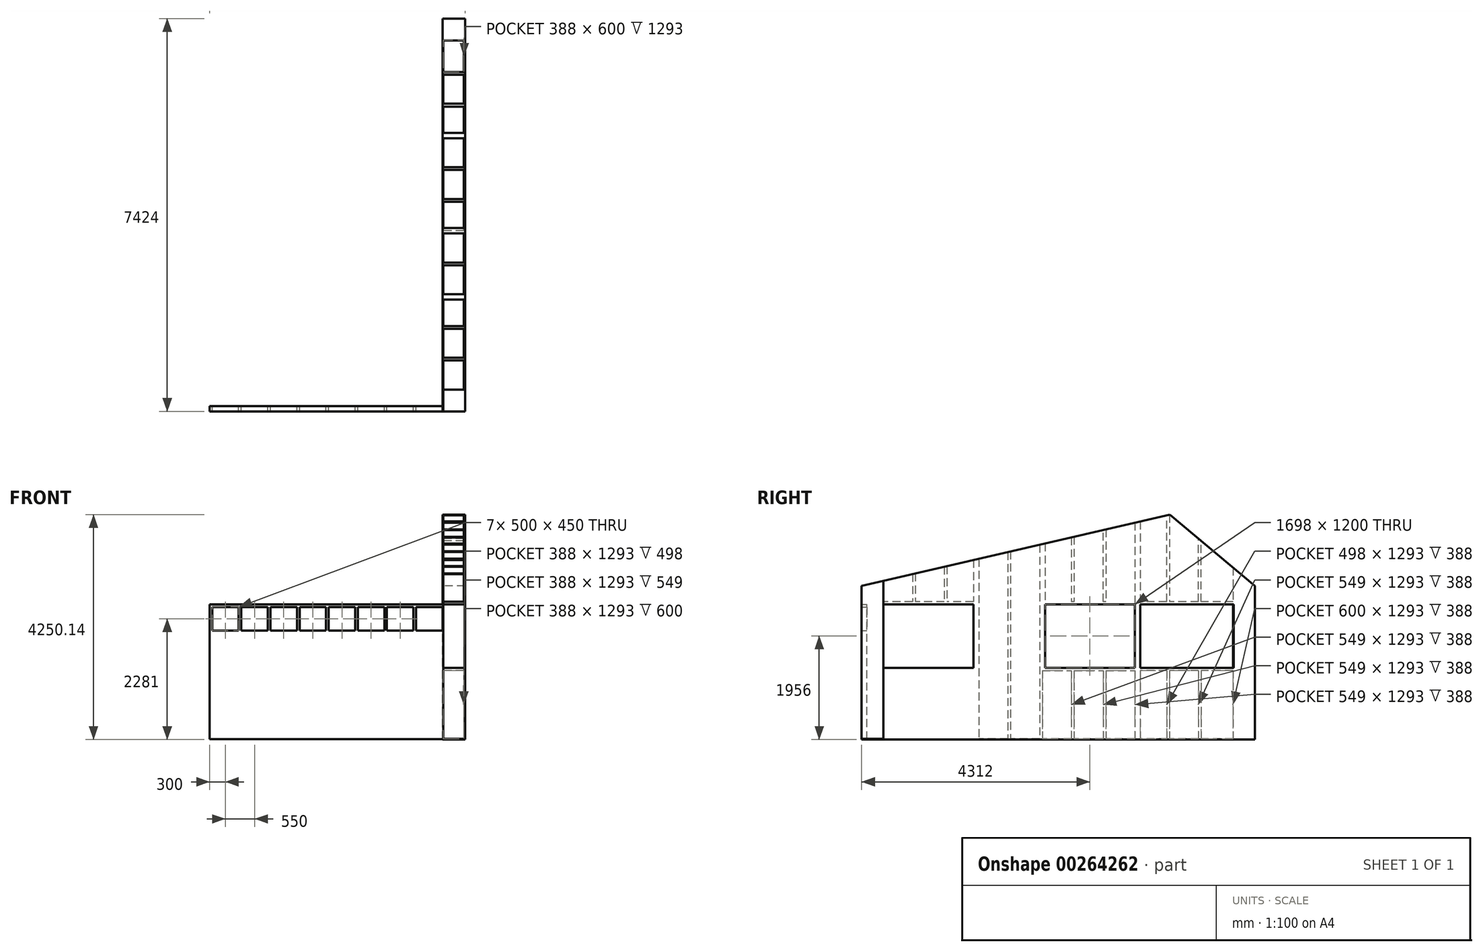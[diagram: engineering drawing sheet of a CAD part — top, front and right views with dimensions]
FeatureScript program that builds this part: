
annotation { "Feature Type Name" : "Feature", "Feature Type Description" : "" }
export const myFeature = defineFeature(function(context is Context, id is Id, definition is map)
    precondition{}
    {
        {
            var Q0;
            Q0=qCreatedBy(makeId("Right.planeOp"),FACE);
            var sketch = newSketch(context, id + "F0", { "sketchPlane" : qUnion([Q0])});
            skLineSegment(sketch, "E0.bottom", {"start": v(0, 0) * mm, "end": v(2161, 0) * mm});
            skLineSegment(sketch, "E0.top", {"start": v(412, 2900) * mm, "end": v(961, 2900) * mm});
            skLineSegment(sketch, "E0.left", {"start": v(0, 0) * mm, "end": v(0, 2900) * mm});
            skLineSegment(sketch, "E0.right", {"start": v(7424, 0) * mm, "end": v(7424, 2900) * mm});
            skLineSegment(sketch, "E1", {"start": v(7424, 2900) * mm, "end": v(5822.11, 4244.14) * mm});
            skLineSegment(sketch, "E2", {"start": v(5822.11, 4244.14) * mm, "end": v(0, 2900) * mm});
            skLineSegment(sketch, "E3", {"start": v(412, 2995.12) * mm, "end": v(412, 0) * mm});
            skLineSegment(sketch, "E4", {"start": v(7012, 3245.7) * mm, "end": v(7012, 0) * mm});
            skLineSegment(sketch, "E5.bottom", {"start": v(961, 2900) * mm, "end": v(1012, 2900) * mm});
            skLineSegment(sketch, "E5.top", {"start": v(961, 0) * mm, "end": v(1012, 0) * mm});
            skLineSegment(sketch, "E5.left", {"start": v(961, 2900) * mm, "end": v(961, 2601) * mm});
            skLineSegment(sketch, "E5.right", {"start": v(1012, 2900) * mm, "end": v(1012, 2601) * mm});
            skLineSegment(sketch, "E6.1.0.0", {"start": v(1561, 2900) * mm, "end": v(1561, 2601) * mm});
            skLineSegment(sketch, "E6.1.0.1", {"start": v(1612, 2900) * mm, "end": v(1612, 2601) * mm});
            skLineSegment(sketch, "E6.1.0.2", {"start": v(1561, 2900) * mm, "end": v(1612, 2900) * mm});
            skLineSegment(sketch, "E6.1.0.3", {"start": v(1561, 0) * mm, "end": v(1612, 0) * mm});
            skLineSegment(sketch, "E6.2.0.0", {"start": v(2161, 2900) * mm, "end": v(2161, 0) * mm});
            skLineSegment(sketch, "E6.2.0.1", {"start": v(2212, 2900) * mm, "end": v(2212, 0) * mm});
            skLineSegment(sketch, "E6.2.0.2", {"start": v(2161, 2900) * mm, "end": v(2212, 2900) * mm});
            skLineSegment(sketch, "E6.2.0.3", {"start": v(2161, 0) * mm, "end": v(2212, 0) * mm});
            skLineSegment(sketch, "E6.3.0.0", {"start": v(2761, 2900) * mm, "end": v(2761, 0) * mm});
            skLineSegment(sketch, "E6.3.0.1", {"start": v(2812, 2900) * mm, "end": v(2812, 0) * mm});
            skLineSegment(sketch, "E6.3.0.2", {"start": v(2761, 2900) * mm, "end": v(2812, 2900) * mm});
            skLineSegment(sketch, "E6.3.0.3", {"start": v(2761, 0) * mm, "end": v(2812, 0) * mm});
            skLineSegment(sketch, "E6.4.0.0", {"start": v(3361, 2900) * mm, "end": v(3361, 0) * mm});
            skLineSegment(sketch, "E6.4.0.1", {"start": v(3412, 3687.72) * mm, "end": v(3412, 0) * mm});
            skLineSegment(sketch, "E6.4.0.2", {"start": v(3361, 2900) * mm, "end": v(3412, 2900) * mm});
            skLineSegment(sketch, "E6.direction1", {"start": v(961, 0) * mm, "end": v(1561, 0) * mm, "construction": true});
            skLineSegment(sketch, "E7", {"start": v(961, 2900) * mm, "end": v(961, 3121.86) * mm});
            skLineSegment(sketch, "E8", {"start": v(961, 3121.86) * mm, "end": v(1012, 3133.64) * mm});
            skLineSegment(sketch, "E9", {"start": v(1012, 3133.64) * mm, "end": v(1012, 2900) * mm});
            skLineSegment(sketch, "E10", {"start": v(1561, 2900) * mm, "end": v(1561, 3260.39) * mm});
            skLineSegment(sketch, "E11", {"start": v(1561, 3260.39) * mm, "end": v(1612, 3272.16) * mm});
            skLineSegment(sketch, "E12", {"start": v(1612, 3272.16) * mm, "end": v(1612, 2900) * mm});
            skLineSegment(sketch, "E13", {"start": v(2161, 2900) * mm, "end": v(2161, 3398.9) * mm});
            skLineSegment(sketch, "E14", {"start": v(2161, 3398.9) * mm, "end": v(2212, 3410.68) * mm});
            skLineSegment(sketch, "E15", {"start": v(2212, 3410.68) * mm, "end": v(2212, 2900) * mm});
            skLineSegment(sketch, "E16", {"start": v(2761, 2900) * mm, "end": v(2761, 3537.43) * mm});
            skLineSegment(sketch, "E17", {"start": v(2761, 3537.43) * mm, "end": v(2812, 3549.2) * mm});
            skLineSegment(sketch, "E18", {"start": v(2812, 3549.2) * mm, "end": v(2812, 2900) * mm});
            skLineSegment(sketch, "E19", {"start": v(3361, 2900) * mm, "end": v(3361, 3675.95) * mm});
            skLineSegment(sketch, "E20", {"start": v(3361, 3675.95) * mm, "end": v(3412, 3687.72) * mm});
            skLineSegment(sketch, "E21", {"start": v(3961, 3814.47) * mm, "end": v(3961, 3814.47) * mm});
            skLineSegment(sketch, "E22", {"start": v(3961, 3814.47) * mm, "end": v(4012, 3826.24) * mm});
            skLineSegment(sketch, "E23", {"start": v(4012, 3826.24) * mm, "end": v(4012, 3826.24) * mm});
            skLineSegment(sketch, "E24.bottom", {"start": v(7012, 0) * mm, "end": v(6412, 0) * mm});
            skLineSegment(sketch, "E25.bottom", {"start": v(2110, 2550) * mm, "end": v(412, 2550) * mm});
            skLineSegment(sketch, "E25.top", {"start": v(2110, 1350) * mm, "end": v(412, 1350) * mm});
            skLineSegment(sketch, "E26.bottom", {"start": v(2110, 2601) * mm, "end": v(412, 2601) * mm});
            skLineSegment(sketch, "E26.top", {"start": v(2110, 1299) * mm, "end": v(412, 1299) * mm});
            skLineSegment(sketch, "E27", {"start": v(2110, 3387.13) * mm, "end": v(2110, 0) * mm});
            skLineSegment(sketch, "E28", {"start": v(4561, 2601) * mm, "end": v(4561, 3952.99) * mm});
            skLineSegment(sketch, "E29", {"start": v(4561, 3952.99) * mm, "end": v(4612, 3964.76) * mm});
            skLineSegment(sketch, "E30", {"start": v(4612, 3964.76) * mm, "end": v(4612, 2601) * mm});
            skLineSegment(sketch, "E31.9.9.0", {"start": v(6361, 0) * mm, "end": v(6412, 0) * mm});
            skLineSegment(sketch, "E32", {"start": v(5761, 2601) * mm, "end": v(5761, 4295.42) * mm});
            skLineSegment(sketch, "E33", {"start": v(6361, 2601) * mm, "end": v(6361, 3791.96) * mm});
            skLineSegment(sketch, "E34", {"start": v(6412, 2601) * mm, "end": v(6412, 3749.17) * mm});
            skLineSegment(sketch, "E35.top", {"start": v(4012, 0) * mm, "end": v(4012, 0) * mm});
            skLineSegment(sketch, "E36.top", {"start": v(7012, 1350) * mm, "end": v(5263, 1350) * mm});
            skLineSegment(sketch, "E37.top", {"start": v(7012, 1299) * mm, "end": v(5263, 1299) * mm});
            skLineSegment(sketch, "E37.left", {"start": v(7012, 2601) * mm, "end": v(7012, 1299) * mm});
            skLineSegment(sketch, "E38.right", {"start": v(4012, 3826.24) * mm, "end": v(4012, 2601) * mm});
            skLineSegment(sketch, "E39.right", {"start": v(5161, 4091.51) * mm, "end": v(5161, 1350) * mm});
            skLineSegment(sketch, "E40", {"start": v(3961, 3814.47) * mm, "end": v(3961, 2601) * mm});
            skLineSegment(sketch, "E41.trimOffspring", {"start": v(4012, 0) * mm, "end": v(7424, 0) * mm});
            skLineSegment(sketch, "E42.trimOffspring", {"start": v(3961, 0) * mm, "end": v(3412, 0) * mm});
            skLineSegment(sketch, "E43.trimOffspring", {"start": v(6361, 0) * mm, "end": v(4012, 0) * mm});
            skLineSegment(sketch, "E44.trimOffspring", {"start": v(3412, 0) * mm, "end": v(3961, 0) * mm});
            skLineSegment(sketch, "E45.trimOffspring", {"start": v(3361, 0) * mm, "end": v(412, 0) * mm});
            skLineSegment(sketch, "E46", {"start": v(3412, 0) * mm, "end": v(3361, 0) * mm});
            skLineSegment(sketch, "E47", {"start": v(4012, 0) * mm, "end": v(3961, 0) * mm});
            skLineSegment(sketch, "E48.trimOffspring", {"start": v(2812, 0) * mm, "end": v(3361, 0) * mm});
            skLineSegment(sketch, "E49.trimOffspring", {"start": v(2212, 0) * mm, "end": v(2761, 0) * mm});
            skLineSegment(sketch, "E50.trimOffspring", {"start": v(6412, 1299) * mm, "end": v(6412, 0) * mm});
            skLineSegment(sketch, "E51.trimOffspring", {"start": v(6361, 1299) * mm, "end": v(6361, 0) * mm});
            skLineSegment(sketch, "E52", {"start": v(5212, 4103.29) * mm, "end": v(5212, 0) * mm});
            skLineSegment(sketch, "E53", {"start": v(5812, 4252.63) * mm, "end": v(5812, 2601) * mm});
            skLineSegment(sketch, "E54.trimOffspring", {"start": v(961, 1299) * mm, "end": v(961, 0) * mm});
            skLineSegment(sketch, "E55.trimOffspring", {"start": v(1012, 1299) * mm, "end": v(1012, 0) * mm});
            skLineSegment(sketch, "E56.trimOffspring", {"start": v(1561, 2900) * mm, "end": v(2110, 2900) * mm});
            skLineSegment(sketch, "E57", {"start": v(5812, 1299) * mm, "end": v(5812, 0) * mm});
            skLineSegment(sketch, "E58", {"start": v(5761, 1299) * mm, "end": v(5761, 0) * mm});
            skLineSegment(sketch, "E59", {"start": v(4612, 2550) * mm, "end": v(4561, 2550) * mm});
            skLineSegment(sketch, "E60", {"start": v(7012, 2601) * mm, "end": v(5263, 2601) * mm});
            skLineSegment(sketch, "E61", {"start": v(7012, 2550) * mm, "end": v(5263, 2550) * mm});
            skLineSegment(sketch, "E62", {"start": v(5212, 2550) * mm, "end": v(3463, 2550) * mm});
            skLineSegment(sketch, "E63", {"start": v(3463, 1350) * mm, "end": v(5161, 1350) * mm});
            skLineSegment(sketch, "E64", {"start": v(5161, 2601) * mm, "end": v(3463, 2601) * mm});
            skLineSegment(sketch, "E65", {"start": v(3412, 1299) * mm, "end": v(5161, 1299) * mm});
            skLineSegment(sketch, "E66", {"start": v(4561, 1299) * mm, "end": v(4561, 0) * mm});
            skLineSegment(sketch, "E67", {"start": v(4612, 1299) * mm, "end": v(4612, 0) * mm});
            skLineSegment(sketch, "E68.trimOffspring", {"start": v(5161, 1299) * mm, "end": v(5161, 0) * mm});
            skLineSegment(sketch, "E69", {"start": v(3412, 1299) * mm, "end": v(3412, 0) * mm});
            skLineSegment(sketch, "E70", {"start": v(3463, 3699.5) * mm, "end": v(3463, 0) * mm});
            skLineSegment(sketch, "E71", {"start": v(5263, 4115.06) * mm, "end": v(5263, 0) * mm});
            skLineSegment(sketch, "E72.trimOffspring", {"start": v(4012, 1299) * mm, "end": v(4012, 0) * mm});
            skLineSegment(sketch, "E73.trimOffspring", {"start": v(3961, 1299) * mm, "end": v(3961, 0) * mm});
            skLineSegment(sketch, "E74.trimOffspring", {"start": v(1612, 1299) * mm, "end": v(1612, 0) * mm});
            skLineSegment(sketch, "E75.trimOffspring", {"start": v(1561, 1299) * mm, "end": v(1561, 0) * mm});
            skSolve(sketch);
        }
        {
            var Q0;
            {var subQ0=sQuery(id+"F0.wireOp",EDGE,"E33");Q0=makeQuery(id+"F0.imprint","IMPRINT",FACE,{"disambiguationData":[TD([[makeQuery(id+"F0.imprint","IMPRINT",EDGE,{"derivedFrom":subQ0}),-1.0]])]});}
            var Q1;
            {var subQ0=sQuery(id+"F0.wireOp",EDGE,"E53");var subQ1=sQuery(id+"F0.wireOp",EDGE,"E2");var subQ2=makeQuery(id+"F0.imprint","INTERSECT",VERTEX,{"derivedFrom":[subQ1,subQ0]});Q1=makeQuery(id+"F0.imprint","IMPRINT",FACE,{"disambiguationData":[TD([[makeQuery(id+"F0.imprint","IMPRINT",EDGE,{"disambiguationData":[TD([[subQ2,-1.0]])],"derivedFrom":subQ1}),1.0]])]});}
            var Q2;
            {var subQ0=sQuery(id+"F0.wireOp",EDGE,"E33");Q2=makeQuery(id+"F0.imprint","IMPRINT",FACE,{"disambiguationData":[TD([[makeQuery(id+"F0.imprint","IMPRINT",EDGE,{"derivedFrom":subQ0}),-1.0]])]});}
            var Q3;
            {var subQ0=sQuery(id+"F0.wireOp",EDGE,"E53");var subQ1=sQuery(id+"F0.wireOp",EDGE,"E2");var subQ2=makeQuery(id+"F0.imprint","INTERSECT",VERTEX,{"derivedFrom":[subQ1,subQ0]});Q3=makeQuery(id+"F0.imprint","IMPRINT",FACE,{"disambiguationData":[TD([[makeQuery(id+"F0.imprint","IMPRINT",EDGE,{"disambiguationData":[TD([[subQ2,-1.0]])],"derivedFrom":subQ1}),1.0]])]});}
            var Q4;
            {var subQ0=sQuery(id+"F0.wireOp",EDGE,"E38.top");Q4=makeQuery(id+"F0.imprint","IMPRINT",FACE,{"disambiguationData":[TD([[makeQuery(id+"F0.imprint","IMPRINT",EDGE,{"derivedFrom":subQ0}),1.0]])]});}
            var Q5;
            {var subQ0=sQuery(id+"F0.wireOp",EDGE,"E38.top");Q5=makeQuery(id+"F0.imprint","IMPRINT",FACE,{"disambiguationData":[TD([[makeQuery(id+"F0.imprint","IMPRINT",EDGE,{"derivedFrom":subQ0}),1.0]])]});}
            var Q6;
            {var subQ0=sQuery(id+"F0.wireOp",EDGE,"E6.2.0.0");Q6=makeQuery(id+"F0.imprint","IMPRINT",FACE,{"disambiguationData":[TD([[makeQuery(id+"F0.imprint","IMPRINT",EDGE,{"derivedFrom":subQ0}),1.0]])]});}
            var Q7;
            {var subQ0=sQuery(id+"F0.wireOp",EDGE,"E6.3.0.0");Q7=makeQuery(id+"F0.imprint","IMPRINT",FACE,{"disambiguationData":[TD([[makeQuery(id+"F0.imprint","IMPRINT",EDGE,{"derivedFrom":subQ0}),1.0]])]});}
            var Q8;
            Q8=makeQuery(id+"F0.imprint","IMPRINT",FACE,{"disambiguationData":[TD([[makeQuery(id+"F0.imprint","IMPRINT",EDGE,{"derivedFrom":sQuery(id+"F0.wireOp",EDGE,"E6.4.0.0")}),1.0]])]});
            var Q9;
            {var subQ0=sQuery(id+"F0.wireOp",EDGE,"E50.trimOffspring");Q9=makeQuery(id+"F0.imprint","IMPRINT",FACE,{"disambiguationData":[TD([[makeQuery(id+"F0.imprint","IMPRINT",EDGE,{"derivedFrom":subQ0}),-1.0]])]});}
            var Q10;
            {var subQ0=sQuery(id+"F0.wireOp",EDGE,"E57");Q10=makeQuery(id+"F0.imprint","IMPRINT",FACE,{"disambiguationData":[TD([[makeQuery(id+"F0.imprint","IMPRINT",EDGE,{"derivedFrom":subQ0}),-1.0]])]});}
            var Q11;
            {var subQ4=sQuery(id+"F0.wireOp",EDGE,"E25.bottom");Q11=makeQuery(id+"F0.imprint","IMPRINT",FACE,{"disambiguationData":[TD([[makeQuery(id+"F0.imprint","IMPRINT",EDGE,{"derivedFrom":subQ4}),-1.0]])]});}
            var Q12;
            {var subQ0=sQuery(id+"F0.wireOp",EDGE,"E5.left");Q12=makeQuery(id+"F0.imprint","IMPRINT",FACE,{"disambiguationData":[TD([[makeQuery(id+"F0.imprint","IMPRINT",EDGE,{"derivedFrom":subQ0}),1.0]])]});}
            var Q13;
            {var subQ0=sQuery(id+"F0.wireOp",EDGE,"E33");Q13=makeQuery(id+"F0.imprint","IMPRINT",FACE,{"disambiguationData":[TD([[makeQuery(id+"F0.imprint","IMPRINT",EDGE,{"derivedFrom":subQ0}),-1.0]])]});}
            var Q14;
            {var subQ0=sQuery(id+"F0.wireOp",EDGE,"E53");var subQ1=sQuery(id+"F0.wireOp",EDGE,"E2");var subQ2=makeQuery(id+"F0.imprint","INTERSECT",VERTEX,{"derivedFrom":[subQ1,subQ0]});Q14=makeQuery(id+"F0.imprint","IMPRINT",FACE,{"disambiguationData":[TD([[makeQuery(id+"F0.imprint","IMPRINT",EDGE,{"disambiguationData":[TD([[subQ2,-1.0]])],"derivedFrom":subQ1}),1.0]])]});}
            var Q15;
            {var subQ0=sQuery(id+"F0.wireOp",EDGE,"E53");var subQ1=sQuery(id+"F0.wireOp",EDGE,"E2");var subQ2=makeQuery(id+"F0.imprint","INTERSECT",VERTEX,{"derivedFrom":[subQ1,subQ0]});Q15=makeQuery(id+"F0.imprint","IMPRINT",FACE,{"disambiguationData":[TD([[makeQuery(id+"F0.imprint","IMPRINT",EDGE,{"disambiguationData":[TD([[subQ2,-1.0]])],"derivedFrom":subQ1}),1.0]])]});}
            var Q16;
            {var subQ0=sQuery(id+"F0.wireOp",EDGE,"E5.left");Q16=makeQuery(id+"F0.imprint","IMPRINT",FACE,{"disambiguationData":[TD([[makeQuery(id+"F0.imprint","IMPRINT",EDGE,{"derivedFrom":subQ0}),1.0]])]});}
            var Q17;
            {var subQ0=sQuery(id+"F0.wireOp",EDGE,"E6.3.0.0");Q17=makeQuery(id+"F0.imprint","IMPRINT",FACE,{"disambiguationData":[TD([[makeQuery(id+"F0.imprint","IMPRINT",EDGE,{"derivedFrom":subQ0}),1.0]])]});}
            var Q18;
            {var subQ0=sQuery(id+"F0.wireOp",EDGE,"E38.top");Q18=makeQuery(id+"F0.imprint","IMPRINT",FACE,{"disambiguationData":[TD([[makeQuery(id+"F0.imprint","IMPRINT",EDGE,{"derivedFrom":subQ0}),1.0]])]});}
            var Q19;
            {var subQ0=sQuery(id+"F0.wireOp",EDGE,"E6.2.0.0");Q19=makeQuery(id+"F0.imprint","IMPRINT",FACE,{"disambiguationData":[TD([[makeQuery(id+"F0.imprint","IMPRINT",EDGE,{"derivedFrom":subQ0}),1.0]])]});}
            var Q20;
            Q20=makeQuery(id+"F0.imprint","IMPRINT",FACE,{"disambiguationData":[TD([[makeQuery(id+"F0.imprint","IMPRINT",EDGE,{"derivedFrom":sQuery(id+"F0.wireOp",EDGE,"E6.4.0.0")}),1.0]])]});
            var Q21;
            {var subQ9=sQuery(id+"F0.wireOp",EDGE,"E6.1.0.1");Q21=makeQuery(id+"F0.imprint","IMPRINT",FACE,{"disambiguationData":[TD([[makeQuery(id+"F0.imprint","IMPRINT",EDGE,{"derivedFrom":subQ9}),-1.0]])]});}
            var Q22;
            {var subQ0=sQuery(id+"F0.wireOp",EDGE,"E5.left");Q22=makeQuery(id+"F0.imprint","IMPRINT",FACE,{"disambiguationData":[TD([[makeQuery(id+"F0.imprint","IMPRINT",EDGE,{"derivedFrom":subQ0}),1.0]])]});}
            var Q23;
            {var subQ0=sQuery(id+"F0.wireOp",EDGE,"E5.left");Q23=makeQuery(id+"F0.imprint","IMPRINT",FACE,{"disambiguationData":[TD([[makeQuery(id+"F0.imprint","IMPRINT",EDGE,{"derivedFrom":subQ0}),1.0]])]});}
            var Q24;
            {var subQ6=sQuery(id+"F0.wireOp",EDGE,"E36.bottom");Q24=makeQuery(id+"F0.imprint","IMPRINT",FACE,{"disambiguationData":[TD([[makeQuery(id+"F0.imprint","IMPRINT",EDGE,{"derivedFrom":subQ6}),-1.0]])]});}
            var Q25;
            {var subQ5=sQuery(id+"F0.wireOp",EDGE,"E39.right");Q25=makeQuery(id+"F0.imprint","IMPRINT",FACE,{"disambiguationData":[TD([[makeQuery(id+"F0.imprint","IMPRINT",EDGE,{"derivedFrom":subQ5}),1.0]])]});}
            var Q26;
            {var subQ0=sQuery(id+"F0.wireOp",EDGE,"E28");Q26=makeQuery(id+"F0.imprint","IMPRINT",FACE,{"disambiguationData":[TD([[makeQuery(id+"F0.imprint","IMPRINT",EDGE,{"derivedFrom":subQ0}),-1.0]])]});}
            var Q27;
            Q27=makeQuery(id+"F0.imprint","IMPRINT",FACE,{"disambiguationData":[TD([[makeQuery(id+"F0.imprint","IMPRINT",EDGE,{"derivedFrom":sQuery(id+"F0.wireOp",EDGE,"E19")}),-1.0]])]});
            var Q28;
            Q28=makeQuery(id+"F0.imprint","IMPRINT",FACE,{"disambiguationData":[TD([[makeQuery(id+"F0.imprint","IMPRINT",EDGE,{"derivedFrom":sQuery(id+"F0.wireOp",EDGE,"E16")}),-1.0]])]});
            var Q29;
            Q29=makeQuery(id+"F0.imprint","IMPRINT",FACE,{"disambiguationData":[TD([[makeQuery(id+"F0.imprint","IMPRINT",EDGE,{"derivedFrom":sQuery(id+"F0.wireOp",EDGE,"E13")}),-1.0]])]});
            var Q30;
            {var subQ0=sQuery(id+"F0.wireOp",EDGE,"E10");Q30=makeQuery(id+"F0.imprint","IMPRINT",FACE,{"disambiguationData":[TD([[makeQuery(id+"F0.imprint","IMPRINT",EDGE,{"derivedFrom":subQ0}),-1.0]])]});}
            var Q31;
            Q31=makeQuery(id+"F0.imprint","IMPRINT",FACE,{"disambiguationData":[TD([[makeQuery(id+"F0.imprint","IMPRINT",EDGE,{"derivedFrom":sQuery(id+"F0.wireOp",EDGE,"E7")}),-1.0]])]});
            var Q32;
            {var subQ0=sQuery(id+"F0.wireOp",EDGE,"E54.trimOffspring");var subQ1=sQuery(id+"F0.wireOp",EDGE,"E25.top");var subQ2=makeQuery(id+"F0.imprint","INTERSECT",VERTEX,{"derivedFrom":[subQ1,subQ0]});Q32=makeQuery(id+"F0.imprint","IMPRINT",FACE,{"disambiguationData":[TD([[makeQuery(id+"F0.imprint","IMPRINT",EDGE,{"disambiguationData":[TD([[subQ2,1.0]])],"derivedFrom":subQ1}),1.0]])]});}
            var Q33;
            {var subQ6=sQuery(id+"F0.wireOp",EDGE,"E36.top");Q33=makeQuery(id+"F0.imprint","IMPRINT",FACE,{"disambiguationData":[TD([[makeQuery(id+"F0.imprint","IMPRINT",EDGE,{"derivedFrom":subQ6}),1.0]])]});}
            var Q34;
            {var subQ1=sQuery(id+"F0.wireOp",EDGE,"E38.right");Q34=makeQuery(id+"F0.imprint","IMPRINT",FACE,{"disambiguationData":[TD([[makeQuery(id+"F0.imprint","IMPRINT",EDGE,{"derivedFrom":subQ1}),-1.0]])]});}
            var Q35;
            {var subQ5=sQuery(id+"F0.wireOp",EDGE,"eVp9e5HD-5BNh-1hee-X5fJ-6oQKKsEmArfJ");Q35=makeQuery(id+"F0.imprint","IMPRINT",FACE,{"disambiguationData":[TD([[makeQuery(id+"F0.imprint","IMPRINT",EDGE,{"derivedFrom":subQ5}),-1.0]])]});}
            var Q36;
            {var subQ0=sQuery(id+"F0.wireOp",EDGE,"E21");Q36=makeQuery(id+"F0.imprint","IMPRINT",FACE,{"disambiguationData":[TD([[makeQuery(id+"F0.imprint","IMPRINT",EDGE,{"derivedFrom":subQ0}),-1.0]])]});}
            var Q37;
            {var subQ0=sQuery(id+"F0.wireOp",EDGE,"E25.top");var subQ1=sQuery(id+"F0.wireOp",EDGE,"E3");var subQ2=makeQuery(id+"F0.imprint","INTERSECT",VERTEX,{"derivedFrom":[subQ1,subQ0]});Q37=makeQuery(id+"F0.imprint","IMPRINT",FACE,{"disambiguationData":[TD([[makeQuery(id+"F0.imprint","IMPRINT",EDGE,{"disambiguationData":[TD([[subQ2,-1.0]])],"derivedFrom":subQ1}),1.0]])]});}
            var Q38;
            {var subQ0=sQuery(id+"F0.wireOp",EDGE,"E55.trimOffspring");var subQ1=sQuery(id+"F0.wireOp",EDGE,"E26.top");var subQ2=makeQuery(id+"F0.imprint","INTERSECT",VERTEX,{"derivedFrom":[subQ1,subQ0]});Q38=makeQuery(id+"F0.imprint","IMPRINT",FACE,{"disambiguationData":[TD([[makeQuery(id+"F0.imprint","IMPRINT",EDGE,{"disambiguationData":[TD([[subQ2,-1.0]])],"derivedFrom":subQ1}),1.0]])]});}
            var Q39;
            {var subQ6=sQuery(id+"F0.wireOp",EDGE,"E61");Q39=makeQuery(id+"F0.imprint","IMPRINT",FACE,{"disambiguationData":[TD([[makeQuery(id+"F0.imprint","IMPRINT",EDGE,{"derivedFrom":subQ6}),-1.0]])]});}
            var Q40;
            {var subQ6=sQuery(id+"F0.wireOp",EDGE,"mPpMvecT-8HcG-p5gy-J8uB-iqQnJEzHNlwV");Q40=makeQuery(id+"F0.imprint","IMPRINT",FACE,{"disambiguationData":[TD([[makeQuery(id+"F0.imprint","IMPRINT",EDGE,{"derivedFrom":subQ6}),-1.0]])]});}
            var Q41;
            {var subQ4=sQuery(id+"F0.wireOp",EDGE,"mPpMvecT-8HcG-p5gy-J8uB-iqQnJEzHNlwV");Q41=makeQuery(id+"F0.imprint","IMPRINT",FACE,{"disambiguationData":[TD([[makeQuery(id+"F0.imprint","IMPRINT",EDGE,{"derivedFrom":subQ4}),1.0]])]});}
            var Q42;
            {var subQ6=sQuery(id+"F0.wireOp",EDGE,"GUthXP1g-z0w5-bO1D-iUhC-Enn5RqslcByq");Q42=makeQuery(id+"F0.imprint","IMPRINT",FACE,{"disambiguationData":[TD([[makeQuery(id+"F0.imprint","IMPRINT",EDGE,{"derivedFrom":subQ6}),-1.0]])]});}
            var Q43;
            {var subQ0=sQuery(id+"F0.wireOp",EDGE,"E68.trimOffspring");Q43=makeQuery(id+"F0.imprint","IMPRINT",FACE,{"disambiguationData":[TD([[makeQuery(id+"F0.imprint","IMPRINT",EDGE,{"derivedFrom":subQ0}),1.0]])]});}
            var Q44;
            {var subQ0=sQuery(id+"F0.wireOp",EDGE,"E66");Q44=makeQuery(id+"F0.imprint","IMPRINT",FACE,{"disambiguationData":[TD([[makeQuery(id+"F0.imprint","IMPRINT",EDGE,{"derivedFrom":subQ0}),1.0]])]});}
            var Q45;
            {var subQ0=sQuery(id+"F0.wireOp",EDGE,"E69");Q45=makeQuery(id+"F0.imprint","IMPRINT",FACE,{"disambiguationData":[TD([[makeQuery(id+"F0.imprint","IMPRINT",EDGE,{"derivedFrom":subQ0}),1.0]])]});}
            var Q46;
            {var subQ9=sQuery(id+"F0.wireOp",EDGE,"E0.right");Q46=makeQuery(id+"F0.imprint","IMPRINT",FACE,{"disambiguationData":[TD([[makeQuery(id+"F0.imprint","IMPRINT",EDGE,{"derivedFrom":subQ9}),1.0]])]});}
            var Q47;
            {var subQ5=sQuery(id+"F0.wireOp",EDGE,"E0.bottom");Q47=makeQuery(id+"F0.imprint","IMPRINT",FACE,{"disambiguationData":[TD([[makeQuery(id+"F0.imprint","IMPRINT",EDGE,{"derivedFrom":subQ5}),1.0]])]});}
            var Q48;
            {var subQ0=sQuery(id+"F0.wireOp",EDGE,"Of8rgk8U-zCIK-7Tz3-qZXN-MONowS2yrxVa");Q48=makeQuery(id+"F0.imprint","IMPRINT",FACE,{"disambiguationData":[TD([[makeQuery(id+"F0.imprint","IMPRINT",EDGE,{"derivedFrom":subQ0}),1.0]])]});}
            var Q49;
            {var subQ5=sQuery(id+"F0.wireOp",EDGE,"Of8rgk8U-zCIK-7Tz3-qZXN-MONowS2yrxVa");Q49=makeQuery(id+"F0.imprint","IMPRINT",FACE,{"disambiguationData":[TD([[makeQuery(id+"F0.imprint","IMPRINT",EDGE,{"derivedFrom":subQ5}),-1.0]])]});}
            var Q50;
            {var subQ0=sQuery(id+"F0.wireOp",EDGE,"E52");var subQ6=sQuery(id+"F0.wireOp",EDGE,"E2");var subQ7=makeQuery(id+"F0.imprint","INTERSECT",VERTEX,{"derivedFrom":[subQ6,subQ0]});Q50=makeQuery(id+"F0.imprint","IMPRINT",FACE,{"disambiguationData":[TD([[makeQuery(id+"F0.imprint","IMPRINT",EDGE,{"disambiguationData":[TD([[subQ7,1.0]])],"derivedFrom":subQ6}),1.0]])]});}
            var Q51;
            {var subQ0=sQuery(id+"F0.wireOp",EDGE,"GUthXP1g-z0w5-bO1D-iUhC-Enn5RqslcByq");Q51=makeQuery(id+"F0.imprint","IMPRINT",FACE,{"disambiguationData":[TD([[makeQuery(id+"F0.imprint","IMPRINT",EDGE,{"derivedFrom":subQ0}),1.0]])]});}
            var Q52;
            {var subQ1=sQuery(id+"F0.wireOp",EDGE,"E62");var subQ4=makeQuery(id+"F0.imprint","IMPRINT",VERTEX,{"disambiguationData":[OD(0.0)],"derivedFrom":subQ1});Q52=makeQuery(id+"F0.imprint","IMPRINT",FACE,{"disambiguationData":[TD([[makeQuery(id+"F0.imprint","IMPRINT",EDGE,{"disambiguationData":[TD([[subQ4,-1.0]])],"derivedFrom":subQ1}),-1.0]])]});}
            var Q53;
            {var subQ3=sQuery(id+"F0.wireOp",EDGE,"E70");var subQ6=makeQuery(id+"F0.imprint","INTERSECT",VERTEX,{"derivedFrom":[sQuery(id+"F0.wireOp",EDGE,"E64"),subQ3]});Q53=makeQuery(id+"F0.imprint","IMPRINT",FACE,{"disambiguationData":[TD([[makeQuery(id+"F0.imprint","IMPRINT",EDGE,{"disambiguationData":[TD([[subQ6,1.0]])],"derivedFrom":subQ3}),-1.0]])]});}
            var Q54;
            Q54=makeQuery(id+"F0.imprint","IMPRINT",FACE,{"disambiguationData":[TD([[makeQuery(id+"F0.imprint","IMPRINT",EDGE,{"derivedFrom":sQuery(id+"F0.wireOp",EDGE,"E47")}),-1.0]])]});
            var Q55;
            {var subQ0=sQuery(id+"F0.wireOp",EDGE,"E74.trimOffspring");Q55=makeQuery(id+"F0.imprint","IMPRINT",FACE,{"disambiguationData":[TD([[makeQuery(id+"F0.imprint","IMPRINT",EDGE,{"derivedFrom":subQ0}),-1.0]])]});}
            var Q56;
            {var subQ6=sQuery(id+"F0.wireOp",EDGE,"E6.2.0.0");Q56=makeQuery(id+"F0.imprint","IMPRINT",FACE,{"disambiguationData":[TD([[makeQuery(id+"F0.imprint","IMPRINT",EDGE,{"derivedFrom":subQ6}),-1.0]])]});}
            extrude(context, id + "F1", {"entities" : qUnion([Q0, Q1, Q2, Q3, Q4, Q5, Q6, Q7, Q8, Q9, Q10, Q11, Q12, Q13, Q14, Q15, Q16, Q17, Q18, Q19, Q20, Q21, Q22, Q23, Q24, Q25, Q26, Q27, Q28, Q29, Q30, Q31, Q32, Q33, Q34, Q35, Q36, Q37, Q38, Q39, Q40, Q41, Q42, Q43, Q44, Q45, Q46, Q47, Q48, Q49, Q50, Q51, Q52, Q53, Q54, Q55, Q56]), "depth" : 400 * mm, "offsetDistance" : 25 * mm});
        }
        {
            var Q0;
            Q0=makeQuery(id+"F1.opExtrude","CAP_FACE",FACE,{"disambiguationData":[OSD([sQuery(id+"F0.wireOp",EDGE,"E0.bottom"),sQuery(id+"F0.wireOp",EDGE,"E0.top"),sQuery(id+"F0.wireOp",EDGE,"E1"),sQuery(id+"F0.wireOp",EDGE,"E2"),sQuery(id+"F0.wireOp",EDGE,"E3"),sQuery(id+"F0.wireOp",EDGE,"E4"),sQuery(id+"F0.wireOp",EDGE,"E5.left"),sQuery(id+"F0.wireOp",EDGE,"E5.right"),sQuery(id+"F0.wireOp",EDGE,"E6.1.0.0"),sQuery(id+"F0.wireOp",EDGE,"E6.2.0.0"),sQuery(id+"F0.wireOp",EDGE,"E6.2.0.1"),sQuery(id+"F0.wireOp",EDGE,"E6.3.0.0"),sQuery(id+"F0.wireOp",EDGE,"E6.3.0.1"),sQuery(id+"F0.wireOp",EDGE,"E6.4.0.0"),sQuery(id+"F0.wireOp",EDGE,"E6.4.0.1"),sQuery(id+"F0.wireOp",EDGE,"E6.5.0.0"),sQuery(id+"F0.wireOp",EDGE,"E6.6.0.0"),sQuery(id+"F0.wireOp",EDGE,"E6.6.0.1"),sQuery(id+"F0.wireOp",EDGE,"E7"),sQuery(id+"F0.wireOp",EDGE,"E8"),sQuery(id+"F0.wireOp",EDGE,"E9"),sQuery(id+"F0.wireOp",EDGE,"E10"),sQuery(id+"F0.wireOp",EDGE,"E11"),sQuery(id+"F0.wireOp",EDGE,"E13"),sQuery(id+"F0.wireOp",EDGE,"E14"),sQuery(id+"F0.wireOp",EDGE,"E15"),sQuery(id+"F0.wireOp",EDGE,"E16"),sQuery(id+"F0.wireOp",EDGE,"E17"),sQuery(id+"F0.wireOp",EDGE,"E18"),sQuery(id+"F0.wireOp",EDGE,"E19"),sQuery(id+"F0.wireOp",EDGE,"E20"),sQuery(id+"F0.wireOp",EDGE,"8VdWadEl-eu3L-hQ6t-bo0H-NKkhGhzPPB04"),sQuery(id+"F0.wireOp",EDGE,"E21"),sQuery(id+"F0.wireOp",EDGE,"E22"),sQuery(id+"F0.wireOp",EDGE,"jDnAEDmB-pTsS-sDcU-dIdj-Oa7KQFsDN3YJ"),sQuery(id+"F0.wireOp",EDGE,"ynP5mbNZ-di9D-vBJM-5H3a-jogifXQtIRLp"),sQuery(id+"F0.wireOp",EDGE,"gObhSo1k-9UGl-B0b9-PoVw-zH8c1aQRmjuj"),sQuery(id+"F0.wireOp",EDGE,"0K7ykxvv-WEkq-RnKF-gthH-UbpIlNLGuIFO"),sQuery(id+"F0.wireOp",EDGE,"Rs4ToZfv-zd40-jkf4-zajj-WmabTFkkZkCH"),sQuery(id+"F0.wireOp",EDGE,"EaJWxrdy-wFjh-rlXd-zm0i-Lc1TIV9AgkaD.left"),sQuery(id+"F0.wireOp",EDGE,"UbQfKujO-wpV6-UaU3-usej-FabyWgDE6CeS.left"),sQuery(id+"F0.wireOp",EDGE,"UbQfKujO-wpV6-UaU3-usej-FabyWgDE6CeS.right"),sQuery(id+"F0.wireOp",EDGE,"9VNBeFEW-eViD-zkEZ-vLSQ-HRV4R9iZ7MZT"),sQuery(id+"F0.wireOp",EDGE,"yBwoAhaT-6PiG-WRAr-1gOz-62lvl0IbkrBI.bottom"),sQuery(id+"F0.wireOp",EDGE,"tzWOEwIv-zt0i-EMHx-hKn9-XnOo8saEgsO4.bottom"),sQuery(id+"F0.wireOp",EDGE,"LlkXUL5w-a4st-GhJx-yION-KIAQrhBNAzwl.bottom"),sQuery(id+"F0.wireOp",EDGE,"LlkXUL5w-a4st-GhJx-yION-KIAQrhBNAzwl.top"),sQuery(id+"F0.wireOp",EDGE,"E24.bottom"),sQuery(id+"F0.wireOp",EDGE,"E24.top"),sQuery(id+"F0.wireOp",EDGE,"E24.left"),sQuery(id+"F0.wireOp",EDGE,"E25.bottom"),sQuery(id+"F0.wireOp",EDGE,"E25.top"),sQuery(id+"F0.wireOp",EDGE,"E25.left"),sQuery(id+"F0.wireOp",EDGE,"E25.right"),sQuery(id+"F0.wireOp",EDGE,"E26.bottom"),sQuery(id+"F0.wireOp",EDGE,"E26.top"),sQuery(id+"F0.wireOp",EDGE,"E26.left"),sQuery(id+"F0.wireOp",EDGE,"E27")])],"isStart":true});
            var sketch = newSketch(context, id + "F2", { "sketchPlane" : qUnion([Q0])});
            skLineSegment(sketch, "E76", {"start": v(0, 0) * mm, "end": v(0, 2900) * mm});
            skLineSegment(sketch, "E77", {"start": v(0, 0) * mm, "end": v(-7424, 0) * mm});
            skLineSegment(sketch, "E78", {"start": v(-7424, 0) * mm, "end": v(-7424, 2900) * mm});
            skLineSegment(sketch, "E79", {"start": v(-7424, 2900) * mm, "end": v(-5822.11, 4244.14) * mm});
            skLineSegment(sketch, "E80", {"start": v(-5822.11, 4244.14) * mm, "end": v(0, 2900) * mm});
            skLineSegment(sketch, "E81", {"start": v(-7012, 3245.7) * mm, "end": v(-7012, 0) * mm});
            skLineSegment(sketch, "E82", {"start": v(-412, 2995.12) * mm, "end": v(-412, 0) * mm});
            skLineSegment(sketch, "E83.bottom", {"start": v(-7012, 2550) * mm, "end": v(-5263, 2550) * mm});
            skLineSegment(sketch, "E83.top", {"start": v(-7012, 1350) * mm, "end": v(-5263, 1350) * mm});
            skLineSegment(sketch, "E83.left", {"start": v(-7012, 2550) * mm, "end": v(-7012, 1350) * mm});
            skLineSegment(sketch, "E83.right", {"start": v(-5263, 2550) * mm, "end": v(-5263, 1350) * mm});
            skLineSegment(sketch, "E84.bottom", {"start": v(-5161, 2550) * mm, "end": v(-3463, 2550) * mm});
            skLineSegment(sketch, "E84.top", {"start": v(-5161, 1350) * mm, "end": v(-3463, 1350) * mm});
            skLineSegment(sketch, "E84.left", {"start": v(-5161, 2550) * mm, "end": v(-5161, 1350) * mm});
            skLineSegment(sketch, "E84.right", {"start": v(-3463, 2550) * mm, "end": v(-3463, 1350) * mm});
            skLineSegment(sketch, "E85.bottom", {"start": v(-2110, 2550) * mm, "end": v(-412, 2550) * mm});
            skLineSegment(sketch, "E85.top", {"start": v(-2110, 1350) * mm, "end": v(-412, 1350) * mm});
            skLineSegment(sketch, "E85.left", {"start": v(-2110, 2550) * mm, "end": v(-2110, 1350) * mm});
            skLineSegment(sketch, "E85.right", {"start": v(-412, 2550) * mm, "end": v(-412, 1350) * mm});
            skSolve(sketch);
        }
        {
            var Q0;
            {var subQ7=sQuery(id+"F0.wireOp",EDGE,"e1818dce-ccd0-4792-8605-8cf13b5c31cf.3.7.0");var subQ8=makeQuery(id+"F1.opExtrude","CAP_EDGE",EDGE,{"disambiguationData":[OSD([subQ7,sQuery(id+"F0.wireOp",EDGE,"1hyhhuAO-2BNj-R4MZ-jLCW-Rz5s6ycj8wrf")])],"isStart":true});Q0=makeQuery(id+"F2.imprint","IMPRINT",FACE,{"disambiguationData":[TD([[makeQuery(id+"F2.imprint","IMPRINT",EDGE,{"derivedFrom":subQ8}),-1.0]])]});}
            var Q1;
            Q1=makeQuery(id+"F2.imprint","IMPRINT",FACE,{"disambiguationData":[TD([[makeQuery(id+"F2.imprint","IMPRINT",EDGE,{"derivedFrom":sQuery(id+"F2.wireOp",EDGE,"ILeUxKm7-PxD1-PjJP-hyR4-TxpfcvWZJf5n")}),-1.0]])]});
            var Q2;
            {var subQ1=sQuery(id+"F0.wireOp",EDGE,"E6.5.0.1");var subQ2=makeQuery(id+"F1.opExtrude","CAP_EDGE",EDGE,{"disambiguationData":[OSD([subQ1,sQuery(id+"F0.wireOp",EDGE,"E23")])],"isStart":true});Q2=makeQuery(id+"F2.imprint","IMPRINT",FACE,{"disambiguationData":[TD([[makeQuery(id+"F2.imprint","IMPRINT",EDGE,{"derivedFrom":subQ2}),-1.0]])]});}
            var Q3;
            {var subQ1=sQuery(id+"F0.wireOp",EDGE,"E6.5.0.0");var subQ2=makeQuery(id+"F1.opExtrude","CAP_EDGE",EDGE,{"disambiguationData":[OSD([subQ1,sQuery(id+"F0.wireOp",EDGE,"E21")])],"isStart":true});Q3=makeQuery(id+"F2.imprint","IMPRINT",FACE,{"disambiguationData":[TD([[makeQuery(id+"F2.imprint","IMPRINT",EDGE,{"derivedFrom":subQ2}),-1.0]])]});}
            var Q4;
            {var subQ1=sQuery(id+"F0.wireOp",EDGE,"E6.3.0.1");var subQ2=makeQuery(id+"F1.opExtrude","CAP_EDGE",EDGE,{"disambiguationData":[OSD([subQ1,sQuery(id+"F0.wireOp",EDGE,"E18")])],"isStart":true});Q4=makeQuery(id+"F2.imprint","IMPRINT",FACE,{"disambiguationData":[TD([[makeQuery(id+"F2.imprint","IMPRINT",EDGE,{"derivedFrom":subQ2}),-1.0]])]});}
            var Q5;
            {var subQ1=sQuery(id+"F0.wireOp",EDGE,"E6.2.0.1");var subQ2=makeQuery(id+"F1.opExtrude","CAP_EDGE",EDGE,{"disambiguationData":[OSD([subQ1,sQuery(id+"F0.wireOp",EDGE,"E15")])],"isStart":true});Q5=makeQuery(id+"F2.imprint","IMPRINT",FACE,{"disambiguationData":[TD([[makeQuery(id+"F2.imprint","IMPRINT",EDGE,{"derivedFrom":subQ2}),-1.0]])]});}
            var Q6;
            {var subQ3=sQuery(id+"F0.wireOp",EDGE,"E27");var subQ4=makeQuery(id+"F1.opExtrude","CAP_EDGE",EDGE,{"disambiguationData":[OSD([subQ3])],"isStart":true});Q6=makeQuery(id+"F2.imprint","IMPRINT",FACE,{"disambiguationData":[TD([[makeQuery(id+"F2.imprint","IMPRINT",EDGE,{"derivedFrom":subQ4}),-1.0]])]});}
            var Q7;
            {var subQ2=sQuery(id+"F0.wireOp",EDGE,"E5.right");Q7=makeQuery(id+"F2.imprint","IMPRINT",FACE,{"disambiguationData":[TD([[makeQuery(id+"F2.imprint","IMPRINT",EDGE,{"derivedFrom":makeQuery(id+"F1.opExtrude","CAP_EDGE",EDGE,{"disambiguationData":[OSD([subQ2])],"isStart":true})}),-1.0]])]});}
            var Q8;
            {var subQ0=sQuery(id+"F0.wireOp",EDGE,"E5.left");Q8=makeQuery(id+"F2.imprint","IMPRINT",FACE,{"disambiguationData":[TD([[makeQuery(id+"F2.imprint","IMPRINT",EDGE,{"derivedFrom":makeQuery(id+"F1.opExtrude","CAP_EDGE",EDGE,{"disambiguationData":[OSD([subQ0])],"isStart":true})}),1.0]])]});}
            var Q9;
            {var subQ0=sQuery(id+"F0.wireOp",EDGE,"E6.5.0.1");Q9=makeQuery(id+"F2.imprint","IMPRINT",FACE,{"disambiguationData":[TD([[makeQuery(id+"F2.imprint","IMPRINT",EDGE,{"derivedFrom":makeQuery(id+"F1.opExtrude","CAP_EDGE",EDGE,{"disambiguationData":[OSD([subQ0])],"isStart":true})}),-1.0]])]});}
            var Q10;
            {var subQ5=sQuery(id+"F0.wireOp",EDGE,"e1818dce-ccd0-4792-8605-8cf13b5c31cf.3.7.0");Q10=makeQuery(id+"F2.imprint","IMPRINT",FACE,{"disambiguationData":[TD([[makeQuery(id+"F2.imprint","IMPRINT",EDGE,{"derivedFrom":makeQuery(id+"F1.opExtrude","CAP_EDGE",EDGE,{"disambiguationData":[OSD([subQ5])],"isStart":true})}),-1.0]])]});}
            var Q11;
            {var subQ0=sQuery(id+"F0.wireOp",EDGE,"e1818dce-ccd0-4792-8605-8cf13b5c31cf.0.7.0");Q11=makeQuery(id+"F2.imprint","IMPRINT",FACE,{"disambiguationData":[TD([[makeQuery(id+"F2.imprint","IMPRINT",EDGE,{"derivedFrom":makeQuery(id+"F1.opExtrude","CAP_EDGE",EDGE,{"disambiguationData":[OSD([subQ0])],"isStart":true})}),1.0]])]});}
            var Q12;
            {var subQ0=sQuery(id+"F2.wireOp",EDGE,"ZMtvcRPi-jAjO-QkiL-2TWF-Vtbn8s9l3dLs");Q12=makeQuery(id+"F2.imprint","IMPRINT",FACE,{"disambiguationData":[TD([[makeQuery(id+"F2.imprint","IMPRINT",EDGE,{"derivedFrom":subQ0}),1.0]])]});}
            var Q13;
            Q13=makeQuery(id+"F2.imprint","IMPRINT",FACE,{"disambiguationData":[TD([[makeQuery(id+"F2.imprint","IMPRINT",EDGE,{"derivedFrom":sQuery(id+"F2.wireOp",EDGE,"uClL61Lv-TRPL-A0ij-AnAf-oDA95NpnLm0b")}),1.0]])]});
            var Q14;
            Q14=makeQuery(id+"F2.imprint","IMPRINT",FACE,{"disambiguationData":[TD([[makeQuery(id+"F2.imprint","IMPRINT",EDGE,{"derivedFrom":sQuery(id+"F2.wireOp",EDGE,"Im6U3rb0-TCcN-t8Da-UMX7-wiPgaS2T3dir.bottom")}),1.0]])]});
            var Q15;
            {var subQ0=sQuery(id+"F2.wireOp",EDGE,"qwQDB58f-RUHw-PsP3-CbaN-XezXBzqP1wrV");var subQ3=sQuery(id+"F2.wireOp",EDGE,"km0tzIaL-IrMw-PDQN-gETX-j8iAy3c5roSj");var subQ4=makeQuery(id+"F2.imprint","INTERSECT",VERTEX,{"derivedFrom":[subQ0,subQ3]});Q15=makeQuery(id+"F2.imprint","IMPRINT",FACE,{"disambiguationData":[TD([[makeQuery(id+"F2.imprint","IMPRINT",EDGE,{"disambiguationData":[TD([[subQ4,1.0]])],"derivedFrom":subQ0}),1.0]])]});}
            var Q16;
            {var subQ3=sQuery(id+"F2.wireOp",EDGE,"9nWFPutj-UhIj-vgEE-YIhj-UoM9MSRTHULn.bottom");Q16=makeQuery(id+"F2.imprint","IMPRINT",FACE,{"disambiguationData":[TD([[makeQuery(id+"F2.imprint","IMPRINT",EDGE,{"derivedFrom":subQ3}),1.0]])]});}
            var Q17;
            Q17=makeQuery(id+"F2.imprint","IMPRINT",FACE,{"disambiguationData":[TD([[makeQuery(id+"F2.imprint","IMPRINT",EDGE,{"derivedFrom":sQuery(id+"F2.wireOp",EDGE,"9nWFPutj-UhIj-vgEE-YIhj-UoM9MSRTHULn.bottom")}),-1.0]])]});
            var Q18;
            Q18=makeQuery(id+"F2.imprint","IMPRINT",FACE,{"disambiguationData":[TD([[makeQuery(id+"F2.imprint","IMPRINT",EDGE,{"derivedFrom":sQuery(id+"F2.wireOp",EDGE,"fYndKTm8-z6r6-5my6-m4xG-jFz9rcoxcGbT")}),1.0]])]});
            var Q19;
            {var subQ0=sQuery(id+"F2.wireOp",EDGE,"L5Ojlj5x-cSsC-0GVV-Gx6i-wFuJb7dHBc9e");Q19=makeQuery(id+"F2.imprint","IMPRINT",FACE,{"disambiguationData":[TD([[makeQuery(id+"F2.imprint","IMPRINT",EDGE,{"derivedFrom":subQ0}),1.0]])]});}
            var Q20;
            {var subQ1=sQuery(id+"F0.wireOp",EDGE,"E6.6.0.1");var subQ2=makeQuery(id+"F1.opExtrude","CAP_EDGE",EDGE,{"disambiguationData":[OSD([subQ1,sQuery(id+"F0.wireOp",EDGE,"E30")])],"isStart":true});Q20=makeQuery(id+"F2.imprint","IMPRINT",FACE,{"disambiguationData":[TD([[makeQuery(id+"F2.imprint","IMPRINT",EDGE,{"derivedFrom":subQ2}),-1.0]])]});}
            var Q21;
            {var subQ2=sQuery(id+"F0.wireOp",EDGE,"E31.3.8.0");Q21=makeQuery(id+"F2.imprint","IMPRINT",FACE,{"disambiguationData":[TD([[makeQuery(id+"F2.imprint","IMPRINT",EDGE,{"derivedFrom":makeQuery(id+"F1.opExtrude","CAP_EDGE",EDGE,{"disambiguationData":[OSD([subQ2])],"isStart":true})}),-1.0]])]});}
            var Q22;
            {var subQ2=sQuery(id+"F0.wireOp",EDGE,"E31.3.9.0");Q22=makeQuery(id+"F2.imprint","IMPRINT",FACE,{"disambiguationData":[TD([[makeQuery(id+"F2.imprint","IMPRINT",EDGE,{"derivedFrom":makeQuery(id+"F1.opExtrude","CAP_EDGE",EDGE,{"disambiguationData":[OSD([subQ2])],"isStart":true})}),-1.0]])]});}
            var Q23;
            Q23=makeQuery(id+"F2.imprint","IMPRINT",FACE,{"disambiguationData":[TD([[makeQuery(id+"F2.imprint","IMPRINT",EDGE,{"derivedFrom":sQuery(id+"F2.wireOp",EDGE,"9nWFPutj-UhIj-vgEE-YIhj-UoM9MSRTHULn.top")}),1.0]])]});
            var Q24;
            {var subQ1=sQuery(id+"F0.wireOp",EDGE,"E34");var subQ2=makeQuery(id+"F1.opExtrude","CAP_EDGE",EDGE,{"disambiguationData":[OSD([subQ1])],"isStart":true});Q24=makeQuery(id+"F2.imprint","IMPRINT",FACE,{"disambiguationData":[TD([[makeQuery(id+"F2.imprint","IMPRINT",EDGE,{"derivedFrom":subQ2}),1.0]])]});}
            var Q25;
            Q25=makeQuery(id+"F2.imprint","IMPRINT",FACE,{"disambiguationData":[TD([[makeQuery(id+"F2.imprint","IMPRINT",EDGE,{"derivedFrom":sQuery(id+"F2.wireOp",EDGE,"QYKnhy2d-5zZ4-VZcH-0nsD-n0vEOzAeBYJB.bottom")}),-1.0]])]});
            var Q26;
            {var subQ0=sQuery(id+"F0.wireOp",EDGE,"E6.6.0.0");Q26=makeQuery(id+"F2.imprint","IMPRINT",FACE,{"disambiguationData":[TD([[makeQuery(id+"F2.imprint","IMPRINT",EDGE,{"derivedFrom":makeQuery(id+"F1.opExtrude","CAP_EDGE",EDGE,{"disambiguationData":[OSD([subQ0])],"isStart":true})}),1.0]])]});}
            var Q27;
            {var subQ1=sQuery(id+"F0.wireOp",EDGE,"E28");var subQ2=makeQuery(id+"F1.opExtrude","CAP_EDGE",EDGE,{"disambiguationData":[OSD([subQ1])],"isStart":true});Q27=makeQuery(id+"F2.imprint","IMPRINT",FACE,{"disambiguationData":[TD([[makeQuery(id+"F2.imprint","IMPRINT",EDGE,{"derivedFrom":subQ2}),-1.0]])]});}
            var Q28;
            {var subQ1=sQuery(id+"F0.wireOp",EDGE,"E33");var subQ2=makeQuery(id+"F1.opExtrude","CAP_EDGE",EDGE,{"disambiguationData":[OSD([subQ1])],"isStart":true});Q28=makeQuery(id+"F2.imprint","IMPRINT",FACE,{"disambiguationData":[TD([[makeQuery(id+"F2.imprint","IMPRINT",EDGE,{"derivedFrom":subQ2}),-1.0]])]});}
            var Q29;
            {var subQ2=sQuery(id+"F0.wireOp",EDGE,"E31.0.9.0");Q29=makeQuery(id+"F2.imprint","IMPRINT",FACE,{"disambiguationData":[TD([[makeQuery(id+"F2.imprint","IMPRINT",EDGE,{"derivedFrom":makeQuery(id+"F1.opExtrude","CAP_EDGE",EDGE,{"disambiguationData":[OSD([subQ2])],"isStart":true})}),1.0]])]});}
            var Q30;
            {var subQ0=sQuery(id+"F0.wireOp",EDGE,"E6.6.0.1");Q30=makeQuery(id+"F2.imprint","IMPRINT",FACE,{"disambiguationData":[TD([[makeQuery(id+"F2.imprint","IMPRINT",EDGE,{"derivedFrom":makeQuery(id+"F1.opExtrude","CAP_EDGE",EDGE,{"disambiguationData":[OSD([subQ0])],"isStart":true})}),-1.0]])]});}
            var Q31;
            {var subQ3=sQuery(id+"F0.wireOp",EDGE,"hia5nyX0-TA8Z-EV9i-aT4O-XqiyuSZ8J15y");Q31=makeQuery(id+"F2.imprint","IMPRINT",FACE,{"disambiguationData":[TD([[makeQuery(id+"F2.imprint","IMPRINT",EDGE,{"derivedFrom":makeQuery(id+"F1.opExtrude","CAP_EDGE",EDGE,{"disambiguationData":[OSD([subQ3])],"isStart":true})}),1.0]])]});}
            var Q32;
            {var subQ3=sQuery(id+"F0.wireOp",EDGE,"E58");Q32=makeQuery(id+"F2.imprint","IMPRINT",FACE,{"disambiguationData":[TD([[makeQuery(id+"F2.imprint","IMPRINT",EDGE,{"derivedFrom":makeQuery(id+"F1.opExtrude","CAP_EDGE",EDGE,{"disambiguationData":[OSD([subQ3])],"isStart":true})}),1.0]])]});}
            var Q33;
            {var subQ0=sQuery(id+"F0.wireOp",EDGE,"E51.trimOffspring");Q33=makeQuery(id+"F2.imprint","IMPRINT",FACE,{"disambiguationData":[TD([[makeQuery(id+"F2.imprint","IMPRINT",EDGE,{"derivedFrom":makeQuery(id+"F1.opExtrude","CAP_EDGE",EDGE,{"disambiguationData":[OSD([subQ0])],"isStart":true})}),1.0]])]});}
            var Q34;
            {var subQ0=sQuery(id+"F0.wireOp",EDGE,"Rs4ToZfv-zd40-jkf4-zajj-WmabTFkkZkCH");Q34=makeQuery(id+"F2.imprint","IMPRINT",FACE,{"disambiguationData":[TD([[makeQuery(id+"F2.imprint","IMPRINT",EDGE,{"derivedFrom":makeQuery(id+"F1.opExtrude","CAP_EDGE",EDGE,{"disambiguationData":[OSD([subQ0])],"isStart":true})}),1.0]])]});}
            var Q35;
            {var subQ6=sQuery(id+"F2.wireOp",EDGE,"ltrXrzrP-09eS-KhfT-j1v6-e6Bh1kycxgVD");Q35=makeQuery(id+"F2.imprint","IMPRINT",FACE,{"disambiguationData":[TD([[makeQuery(id+"F2.imprint","IMPRINT",EDGE,{"derivedFrom":subQ6}),-1.0]])]});}
            var Q36;
            {var subQ5=sQuery(id+"F0.wireOp",EDGE,"E55.trimOffspring");Q36=makeQuery(id+"F2.imprint","IMPRINT",FACE,{"disambiguationData":[TD([[makeQuery(id+"F2.imprint","IMPRINT",EDGE,{"derivedFrom":makeQuery(id+"F1.opExtrude","CAP_EDGE",EDGE,{"disambiguationData":[OSD([subQ5])],"isStart":true})}),-1.0]])]});}
            var Q37;
            Q37=makeQuery(id+"F2.imprint","IMPRINT",FACE,{"disambiguationData":[TD([[makeQuery(id+"F2.imprint","IMPRINT",EDGE,{"derivedFrom":sQuery(id+"F2.wireOp",EDGE,"d05e9QIq-D4C1-AxKu-CPFI-rBy6B71EjM0N.bottom")}),1.0]])]});
            var Q38;
            {var subQ1=sQuery(id+"F0.wireOp",EDGE,"E32");var subQ4=makeQuery(id+"F1.opExtrude","CAP_EDGE",EDGE,{"disambiguationData":[OSD([subQ1])],"isStart":true});Q38=makeQuery(id+"F2.imprint","IMPRINT",FACE,{"disambiguationData":[TD([[makeQuery(id+"F2.imprint","IMPRINT",EDGE,{"derivedFrom":subQ4}),-1.0]])]});}
            var Q39;
            {var subQ1=sQuery(id+"F2.wireOp",EDGE,"E78");Q39=makeQuery(id+"F2.imprint","IMPRINT",FACE,{"disambiguationData":[TD([[makeQuery(id+"F2.imprint","IMPRINT",EDGE,{"derivedFrom":subQ1}),-1.0]])]});}
            var Q40;
            {var subQ8=sQuery(id+"F2.wireOp",EDGE,"E85.bottom");Q40=makeQuery(id+"F2.imprint","IMPRINT",FACE,{"disambiguationData":[TD([[makeQuery(id+"F2.imprint","IMPRINT",EDGE,{"derivedFrom":subQ8}),1.0]])]});}
            var Q41;
            {var subQ6=sQuery(id+"F2.wireOp",EDGE,"E76");Q41=makeQuery(id+"F2.imprint","IMPRINT",FACE,{"disambiguationData":[TD([[makeQuery(id+"F2.imprint","IMPRINT",EDGE,{"derivedFrom":subQ6}),1.0]])]});}
            var Q42;
            {var subQ1=sQuery(id+"F0.wireOp",EDGE,"E54.trimOffspring");var subQ2=makeQuery(id+"F1.opExtrude","CAP_EDGE",EDGE,{"disambiguationData":[OSD([subQ1])],"isStart":true});Q42=makeQuery(id+"F2.imprint","IMPRINT",FACE,{"disambiguationData":[TD([[makeQuery(id+"F2.imprint","IMPRINT",EDGE,{"derivedFrom":subQ2}),1.0]])]});}
            var Q43;
            {var subQ5=sQuery(id+"F0.wireOp",EDGE,"E74.trimOffspring");var subQ6=makeQuery(id+"F1.opExtrude","CAP_EDGE",EDGE,{"disambiguationData":[OSD([subQ5])],"isStart":true});Q43=makeQuery(id+"F2.imprint","IMPRINT",FACE,{"disambiguationData":[TD([[makeQuery(id+"F2.imprint","IMPRINT",EDGE,{"derivedFrom":subQ6}),-1.0]])]});}
            var Q44;
            {var subQ1=sQuery(id+"F0.wireOp",EDGE,"E6.1.0.1");var subQ2=makeQuery(id+"F1.opExtrude","CAP_EDGE",EDGE,{"disambiguationData":[OSD([subQ1,sQuery(id+"F0.wireOp",EDGE,"E12")])],"isStart":true});Q44=makeQuery(id+"F2.imprint","IMPRINT",FACE,{"disambiguationData":[TD([[makeQuery(id+"F2.imprint","IMPRINT",EDGE,{"derivedFrom":subQ2}),-1.0]])]});}
            extrude(context, id + "F3", {"entities" : qUnion([Q0, Q1, Q2, Q3, Q4, Q5, Q6, Q7, Q8, Q9, Q10, Q11, Q12, Q13, Q14, Q15, Q16, Q17, Q18, Q19, Q20, Q21, Q22, Q23, Q24, Q25, Q26, Q27, Q28, Q29, Q30, Q31, Q32, Q33, Q34, Q35, Q36, Q37, Q38, Q39, Q40, Q41, Q42, Q43, Q44]), "operationType" : NewBodyOperationType.ADD, "depth" : 12 * mm, "offsetDistance" : 25 * mm});
        }
        {
            var Q0;
            Q0=makeQuery(id+"F1.opExtrude","CAP_FACE",FACE,{"disambiguationData":[OSD([sQuery(id+"F0.wireOp",EDGE,"E0.bottom"),sQuery(id+"F0.wireOp",EDGE,"E0.top"),sQuery(id+"F0.wireOp",EDGE,"E1"),sQuery(id+"F0.wireOp",EDGE,"E2"),sQuery(id+"F0.wireOp",EDGE,"E3"),sQuery(id+"F0.wireOp",EDGE,"E4"),sQuery(id+"F0.wireOp",EDGE,"E5.left"),sQuery(id+"F0.wireOp",EDGE,"E5.right"),sQuery(id+"F0.wireOp",EDGE,"E6.1.0.0"),sQuery(id+"F0.wireOp",EDGE,"E6.2.0.0"),sQuery(id+"F0.wireOp",EDGE,"E6.2.0.1"),sQuery(id+"F0.wireOp",EDGE,"E6.3.0.0"),sQuery(id+"F0.wireOp",EDGE,"E6.3.0.1"),sQuery(id+"F0.wireOp",EDGE,"E6.4.0.0"),sQuery(id+"F0.wireOp",EDGE,"E6.4.0.1"),sQuery(id+"F0.wireOp",EDGE,"E6.5.0.0"),sQuery(id+"F0.wireOp",EDGE,"E6.6.0.0"),sQuery(id+"F0.wireOp",EDGE,"E6.6.0.1"),sQuery(id+"F0.wireOp",EDGE,"E7"),sQuery(id+"F0.wireOp",EDGE,"E8"),sQuery(id+"F0.wireOp",EDGE,"E9"),sQuery(id+"F0.wireOp",EDGE,"E10"),sQuery(id+"F0.wireOp",EDGE,"E11"),sQuery(id+"F0.wireOp",EDGE,"E13"),sQuery(id+"F0.wireOp",EDGE,"E14"),sQuery(id+"F0.wireOp",EDGE,"E15"),sQuery(id+"F0.wireOp",EDGE,"E16"),sQuery(id+"F0.wireOp",EDGE,"E17"),sQuery(id+"F0.wireOp",EDGE,"E18"),sQuery(id+"F0.wireOp",EDGE,"E19"),sQuery(id+"F0.wireOp",EDGE,"E20"),sQuery(id+"F0.wireOp",EDGE,"8VdWadEl-eu3L-hQ6t-bo0H-NKkhGhzPPB04"),sQuery(id+"F0.wireOp",EDGE,"E21"),sQuery(id+"F0.wireOp",EDGE,"E22"),sQuery(id+"F0.wireOp",EDGE,"jDnAEDmB-pTsS-sDcU-dIdj-Oa7KQFsDN3YJ"),sQuery(id+"F0.wireOp",EDGE,"ynP5mbNZ-di9D-vBJM-5H3a-jogifXQtIRLp"),sQuery(id+"F0.wireOp",EDGE,"gObhSo1k-9UGl-B0b9-PoVw-zH8c1aQRmjuj"),sQuery(id+"F0.wireOp",EDGE,"0K7ykxvv-WEkq-RnKF-gthH-UbpIlNLGuIFO"),sQuery(id+"F0.wireOp",EDGE,"Rs4ToZfv-zd40-jkf4-zajj-WmabTFkkZkCH"),sQuery(id+"F0.wireOp",EDGE,"EaJWxrdy-wFjh-rlXd-zm0i-Lc1TIV9AgkaD.left"),sQuery(id+"F0.wireOp",EDGE,"UbQfKujO-wpV6-UaU3-usej-FabyWgDE6CeS.left"),sQuery(id+"F0.wireOp",EDGE,"UbQfKujO-wpV6-UaU3-usej-FabyWgDE6CeS.right"),sQuery(id+"F0.wireOp",EDGE,"9VNBeFEW-eViD-zkEZ-vLSQ-HRV4R9iZ7MZT"),sQuery(id+"F0.wireOp",EDGE,"yBwoAhaT-6PiG-WRAr-1gOz-62lvl0IbkrBI.bottom"),sQuery(id+"F0.wireOp",EDGE,"tzWOEwIv-zt0i-EMHx-hKn9-XnOo8saEgsO4.bottom"),sQuery(id+"F0.wireOp",EDGE,"LlkXUL5w-a4st-GhJx-yION-KIAQrhBNAzwl.bottom"),sQuery(id+"F0.wireOp",EDGE,"LlkXUL5w-a4st-GhJx-yION-KIAQrhBNAzwl.top"),sQuery(id+"F0.wireOp",EDGE,"E24.bottom"),sQuery(id+"F0.wireOp",EDGE,"E24.top"),sQuery(id+"F0.wireOp",EDGE,"E24.left"),sQuery(id+"F0.wireOp",EDGE,"E25.bottom"),sQuery(id+"F0.wireOp",EDGE,"E25.top"),sQuery(id+"F0.wireOp",EDGE,"E25.left"),sQuery(id+"F0.wireOp",EDGE,"E25.right"),sQuery(id+"F0.wireOp",EDGE,"E26.bottom"),sQuery(id+"F0.wireOp",EDGE,"E26.top"),sQuery(id+"F0.wireOp",EDGE,"E26.left"),sQuery(id+"F0.wireOp",EDGE,"E27")])],"isStart":false});
            var sketch = newSketch(context, id + "F4", { "sketchPlane" : qUnion([Q0])});
            skLineSegment(sketch, "E86", {"start": v(0, 0) * mm, "end": v(7424, 0) * mm});
            skLineSegment(sketch, "E87", {"start": v(7424, 0) * mm, "end": v(7424, 2900) * mm});
            skLineSegment(sketch, "E88", {"start": v(7424, 2900) * mm, "end": v(5822.11, 4244.14) * mm});
            skLineSegment(sketch, "E89", {"start": v(0, 2900) * mm, "end": v(5822.11, 4244.14) * mm});
            skLineSegment(sketch, "E90", {"start": v(0, 2900) * mm, "end": v(0, 0) * mm});
            skLineSegment(sketch, "E91", {"start": v(7024, 3235.64) * mm, "end": v(7024, 1350) * mm});
            skLineSegment(sketch, "E92.bottom", {"start": v(3463, 2550) * mm, "end": v(5161, 2550) * mm});
            skLineSegment(sketch, "E92.top", {"start": v(3463, 1350) * mm, "end": v(5161, 1350) * mm});
            skLineSegment(sketch, "E92.left", {"start": v(3463, 2550) * mm, "end": v(3463, 1350) * mm});
            skLineSegment(sketch, "E92.right", {"start": v(5161, 2550) * mm, "end": v(5161, 1350) * mm});
            skLineSegment(sketch, "E93.bottom", {"start": v(7024, 2550) * mm, "end": v(5263, 2550) * mm});
            skLineSegment(sketch, "E93.top", {"start": v(7024, 1350) * mm, "end": v(5263, 1350) * mm});
            skLineSegment(sketch, "E93.left", {"start": v(7024, 2550) * mm, "end": v(7024, 1350) * mm});
            skLineSegment(sketch, "E93.right", {"start": v(5263, 2550) * mm, "end": v(5263, 1350) * mm});
            skLineSegment(sketch, "E94", {"start": v(412, 0) * mm, "end": v(412, 2995.12) * mm});
            skLineSegment(sketch, "E95.bottom", {"start": v(2110, 2550) * mm, "end": v(412, 2550) * mm});
            skLineSegment(sketch, "E95.top", {"start": v(2110, 1350) * mm, "end": v(412, 1350) * mm});
            skLineSegment(sketch, "E95.left", {"start": v(2110, 2550) * mm, "end": v(2110, 1350) * mm});
            skLineSegment(sketch, "E95.right", {"start": v(412, 2550) * mm, "end": v(412, 1350) * mm});
            skSolve(sketch);
        }
        {
            var Q0;
            {var subQ11=sQuery(id+"F4.wireOp",EDGE,"B5mqeGFc-T6t6-RReW-t24S-Dyp4kYL9mOSS.bottom");Q0=makeQuery(id+"F4.imprint","IMPRINT",FACE,{"disambiguationData":[TD([[makeQuery(id+"F4.imprint","IMPRINT",EDGE,{"derivedFrom":subQ11}),-1.0]])]});}
            var Q1;
            {var subQ4=sQuery(id+"F0.wireOp",EDGE,"E6.1.0.0");var subQ5=sQuery(id+"F0.wireOp",EDGE,"E26.top");var subQ6=makeQuery(id+"F0.imprint","INTERSECT",VERTEX,{"derivedFrom":[subQ4,subQ5]});var subQ9=makeQuery(id+"F1.opExtrude","CAP_EDGE",EDGE,{"disambiguationData":[OSD([subQ5]),TDD([makeQuery(id+"F0.imprint","IMPRINT",EDGE,{"disambiguationData":[TD([[subQ6,-1.0]])],"derivedFrom":subQ5})])],"isStart":false});Q1=makeQuery(id+"F4.imprint","IMPRINT",FACE,{"disambiguationData":[TD([[makeQuery(id+"F4.imprint","IMPRINT",EDGE,{"derivedFrom":subQ9}),1.0]])]});}
            var Q2;
            {var subQ2=sQuery(id+"F0.wireOp",EDGE,"E3");var subQ3=sQuery(id+"F0.wireOp",EDGE,"E26.top");var subQ4=makeQuery(id+"F0.imprint","INTERSECT",VERTEX,{"derivedFrom":[subQ2,subQ3]});var subQ9=makeQuery(id+"F1.opExtrude","CAP_EDGE",EDGE,{"disambiguationData":[OSD([subQ3]),TDD([makeQuery(id+"F0.imprint","IMPRINT",EDGE,{"disambiguationData":[TD([[subQ4,1.0]])],"derivedFrom":subQ3})])],"isStart":false});Q2=makeQuery(id+"F4.imprint","IMPRINT",FACE,{"disambiguationData":[TD([[makeQuery(id+"F4.imprint","IMPRINT",EDGE,{"derivedFrom":subQ9}),1.0]])]});}
            var Q3;
            {var subQ1=sQuery(id+"F0.wireOp",EDGE,"E5.right");var subQ2=makeQuery(id+"F1.opExtrude","CAP_EDGE",EDGE,{"disambiguationData":[OSD([subQ1,sQuery(id+"F0.wireOp",EDGE,"E9")])],"isStart":false});Q3=makeQuery(id+"F4.imprint","IMPRINT",FACE,{"disambiguationData":[TD([[makeQuery(id+"F4.imprint","IMPRINT",EDGE,{"derivedFrom":subQ2}),1.0]])]});}
            var Q4;
            {var subQ3=sQuery(id+"F0.wireOp",EDGE,"E5.left");var subQ4=makeQuery(id+"F1.opExtrude","CAP_EDGE",EDGE,{"disambiguationData":[OSD([subQ3,sQuery(id+"F0.wireOp",EDGE,"E7")])],"isStart":false});Q4=makeQuery(id+"F4.imprint","IMPRINT",FACE,{"disambiguationData":[TD([[makeQuery(id+"F4.imprint","IMPRINT",EDGE,{"derivedFrom":subQ4}),-1.0]])]});}
            var Q5;
            {var subQ14=sQuery(id+"F4.wireOp",EDGE,"B5mqeGFc-T6t6-RReW-t24S-Dyp4kYL9mOSS.left");Q5=makeQuery(id+"F4.imprint","IMPRINT",FACE,{"disambiguationData":[TD([[makeQuery(id+"F4.imprint","IMPRINT",EDGE,{"derivedFrom":subQ14}),-1.0]])]});}
            var Q6;
            {var subQ6=sQuery(id+"F4.wireOp",EDGE,"B5mqeGFc-T6t6-RReW-t24S-Dyp4kYL9mOSS.top");Q6=makeQuery(id+"F4.imprint","IMPRINT",FACE,{"disambiguationData":[TD([[makeQuery(id+"F4.imprint","IMPRINT",EDGE,{"derivedFrom":subQ6}),1.0]])]});}
            var Q7;
            {var subQ1=sQuery(id+"F0.wireOp",EDGE,"E6.1.0.1");var subQ2=makeQuery(id+"F1.opExtrude","CAP_EDGE",EDGE,{"disambiguationData":[OSD([subQ1,sQuery(id+"F0.wireOp",EDGE,"E12")])],"isStart":false});Q7=makeQuery(id+"F4.imprint","IMPRINT",FACE,{"disambiguationData":[TD([[makeQuery(id+"F4.imprint","IMPRINT",EDGE,{"derivedFrom":subQ2}),1.0]])]});}
            var Q8;
            {var subQ33=sQuery(id+"F4.wireOp",EDGE,"E95.bottom");Q8=makeQuery(id+"F4.imprint","IMPRINT",FACE,{"disambiguationData":[TD([[makeQuery(id+"F4.imprint","IMPRINT",EDGE,{"derivedFrom":subQ33}),-1.0]])]});}
            var Q9;
            {var subQ5=sQuery(id+"F4.wireOp",EDGE,"E87");Q9=makeQuery(id+"F4.imprint","IMPRINT",FACE,{"disambiguationData":[TD([[makeQuery(id+"F4.imprint","IMPRINT",EDGE,{"derivedFrom":subQ5}),1.0]])]});}
            var Q10;
            {var subQ6=sQuery(id+"F4.wireOp",EDGE,"E90");Q10=makeQuery(id+"F4.imprint","IMPRINT",FACE,{"disambiguationData":[TD([[makeQuery(id+"F4.imprint","IMPRINT",EDGE,{"derivedFrom":subQ6}),-1.0]])]});}
            extrude(context, id + "F5", {"entities" : qUnion([Q0, Q1, Q2, Q3, Q4, Q5, Q6, Q7, Q8, Q9, Q10]), "operationType" : NewBodyOperationType.ADD, "depth" : 24 * mm, "offsetDistance" : 25 * mm, "symmetric" : true});
        }
        {
            var Q0;
            {var subQ0=sQuery(id+"F0.wireOp",EDGE,"E45.trimOffspring");var subQ1=makeQuery(id+"F0.imprint","INTERSECT",VERTEX,{"derivedFrom":[sQuery(id+"F0.wireOp",EDGE,"E6.1.0.1"),subQ0]});var subQ2=sQuery(id+"F0.wireOp",EDGE,"E49.trimOffspring");var subQ3=sQuery(id+"F0.wireOp",EDGE,"E43.trimOffspring");var subQ4=makeQuery(id+"F0.imprint","INTERSECT",VERTEX,{"derivedFrom":[sQuery(id+"F0.wireOp",EDGE,"E39.right"),subQ3]});Q0=makeQuery(id+"F3.boolean.opBoolean","MERGE",FACE,{"derivedFrom":[makeQuery(id+"F1.opExtrude","SWEPT_FACE",FACE,{"disambiguationData":[OSD([sQuery(id+"F0.wireOp",EDGE,"E41.trimOffspring")])]}),makeQuery(id+"F1.opExtrude","SWEPT_FACE",FACE,{"disambiguationData":[OSD([subQ3]),TDD([makeQuery(id+"F0.imprint","IMPRINT",EDGE,{"disambiguationData":[TD([[makeQuery(id+"F0.imprint","INTERSECT",VERTEX,{"derivedFrom":[subQ3,sQuery(id+"F0.wireOp",EDGE,"E57")]}),-1.0]])],"derivedFrom":subQ3})])]}),makeQuery(id+"F1.opExtrude","SWEPT_FACE",FACE,{"disambiguationData":[OSD([subQ3]),TDD([makeQuery(id+"F0.imprint","IMPRINT",EDGE,{"disambiguationData":[TD([[subQ4,1.0]])],"derivedFrom":subQ3}),makeQuery(id+"F0.imprint","IMPRINT",EDGE,{"disambiguationData":[TD([[makeQuery(id+"F0.imprint","INTERSECT",VERTEX,{"derivedFrom":[sQuery(id+"F0.wireOp",EDGE,"E39.left"),subQ3]}),1.0]])],"derivedFrom":subQ3})])]}),makeQuery(id+"F1.opExtrude","SWEPT_FACE",FACE,{"disambiguationData":[OSD([subQ0]),TDD([makeQuery(id+"F0.imprint","IMPRINT",EDGE,{"disambiguationData":[TD([[makeQuery(id+"F0.imprint","INTERSECT",VERTEX,{"derivedFrom":[sQuery(id+"F0.wireOp",EDGE,"E6.3.0.0"),subQ0,subQ2]}),1.0]])],"derivedFrom":subQ0})])]}),makeQuery(id+"F1.opExtrude","SWEPT_FACE",FACE,{"disambiguationData":[OSD([subQ0]),TDD([makeQuery(id+"F0.imprint","IMPRINT",EDGE,{"disambiguationData":[TD([[makeQuery(id+"F0.imprint","INTERSECT",VERTEX,{"derivedFrom":[sQuery(id+"F0.wireOp",EDGE,"E6.2.0.0"),subQ0]}),1.0]])],"derivedFrom":subQ0})])]}),makeQuery(id+"F1.opExtrude","SWEPT_FACE",FACE,{"disambiguationData":[OSD([subQ0]),TDD([makeQuery(id+"F0.imprint","IMPRINT",EDGE,{"disambiguationData":[TD([[subQ1,1.0]])],"derivedFrom":subQ0}),makeQuery(id+"F0.imprint","IMPRINT",EDGE,{"disambiguationData":[TD([[makeQuery(id+"F0.imprint","INTERSECT",VERTEX,{"derivedFrom":[sQuery(id+"F0.wireOp",EDGE,"E6.1.0.0"),subQ0]}),1.0]])],"derivedFrom":subQ0})])]}),makeQuery(id+"F1.opExtrude","SWEPT_FACE",FACE,{"disambiguationData":[OSD([subQ0]),TDD([makeQuery(id+"F0.imprint","IMPRINT",EDGE,{"disambiguationData":[TD([[makeQuery(id+"F0.imprint","INTERSECT",VERTEX,{"derivedFrom":[subQ0,sQuery(id+"F0.wireOp",EDGE,"E54.trimOffspring")]}),1.0]])],"derivedFrom":subQ0})])]}),makeQuery(id+"F1.opExtrude","SWEPT_FACE",FACE,{"disambiguationData":[OSD([sQuery(id+"F0.wireOp",EDGE,"E46")])]}),makeQuery(id+"F1.opExtrude","SWEPT_FACE",FACE,{"disambiguationData":[OSD([sQuery(id+"F0.wireOp",EDGE,"E47")])]}),makeQuery(id+"F3.opExtrude","SWEPT_FACE",FACE,{"disambiguationData":[OSD([sQuery(id+"F2.wireOp",EDGE,"E77")])]})]});}
            var sketch = newSketch(context, id + "F6", { "sketchPlane" : qUnion([Q0])});
            skLineSegment(sketch, "E96.bottom", {"start": v(0, 0) * mm, "end": v(412, 0) * mm});
            skLineSegment(sketch, "E96.top", {"start": v(0, -7424) * mm, "end": v(412, -7424) * mm});
            skLineSegment(sketch, "E96.left", {"start": v(0, 0) * mm, "end": v(0, -7424) * mm});
            skLineSegment(sketch, "E96.right", {"start": v(412, 0) * mm, "end": v(412, -7424) * mm});
            skSolve(sketch);
        }
        {
            var Q0;
            {var subQ0=sQuery(id+"F6.wireOp",EDGE,"E96.bottom");Q0=makeQuery(id+"F6.imprint","IMPRINT",FACE,{"disambiguationData":[TD([[makeQuery(id+"F6.imprint","IMPRINT",EDGE,{"derivedFrom":subQ0}),-1.0]])]});}
            var Q1;
            {var subQ1=sQuery(id+"F0.wireOp",EDGE,"E45.trimOffspring");var subQ2=makeQuery(id+"F1.opExtrude","SWEPT_EDGE",EDGE,{"disambiguationData":[OSD([sQuery(id+"F0.wireOp",EDGE,"E6.1.0.0"),subQ1])]});Q1=makeQuery(id+"F6.imprint","IMPRINT",FACE,{"disambiguationData":[TD([[makeQuery(id+"F6.imprint","IMPRINT",EDGE,{"derivedFrom":subQ2}),-1.0]])]});}
            var Q2;
            {var subQ1=sQuery(id+"F0.wireOp",EDGE,"E45.trimOffspring");var subQ2=makeQuery(id+"F1.opExtrude","SWEPT_EDGE",EDGE,{"disambiguationData":[OSD([sQuery(id+"F0.wireOp",EDGE,"E6.2.0.0"),subQ1])]});Q2=makeQuery(id+"F6.imprint","IMPRINT",FACE,{"disambiguationData":[TD([[makeQuery(id+"F6.imprint","IMPRINT",EDGE,{"derivedFrom":subQ2}),-1.0]])]});}
            var Q3;
            {var subQ1=sQuery(id+"F0.wireOp",EDGE,"E49.trimOffspring");var subQ2=sQuery(id+"F0.wireOp",EDGE,"E45.trimOffspring");var subQ3=makeQuery(id+"F1.opExtrude","SWEPT_EDGE",EDGE,{"disambiguationData":[OSD([sQuery(id+"F0.wireOp",EDGE,"E6.2.0.1"),subQ2,subQ1])]});Q3=makeQuery(id+"F6.imprint","IMPRINT",FACE,{"disambiguationData":[TD([[makeQuery(id+"F6.imprint","IMPRINT",EDGE,{"derivedFrom":subQ3}),1.0]])]});}
            var Q4;
            {var subQ1=sQuery(id+"F0.wireOp",EDGE,"E48.trimOffspring");var subQ2=makeQuery(id+"F1.opExtrude","SWEPT_EDGE",EDGE,{"disambiguationData":[OSD([sQuery(id+"F0.wireOp",EDGE,"E6.3.0.1"),sQuery(id+"F0.wireOp",EDGE,"E45.trimOffspring"),subQ1])]});Q4=makeQuery(id+"F6.imprint","IMPRINT",FACE,{"disambiguationData":[TD([[makeQuery(id+"F6.imprint","IMPRINT",EDGE,{"derivedFrom":subQ2}),1.0]])]});}
            var Q5;
            {var subQ1=sQuery(id+"F0.wireOp",EDGE,"E44.trimOffspring");var subQ2=makeQuery(id+"F1.opExtrude","SWEPT_EDGE",EDGE,{"disambiguationData":[OSD([sQuery(id+"F0.wireOp",EDGE,"E6.4.0.1"),subQ1,sQuery(id+"F0.wireOp",EDGE,"E46")])]});Q5=makeQuery(id+"F6.imprint","IMPRINT",FACE,{"disambiguationData":[TD([[makeQuery(id+"F6.imprint","IMPRINT",EDGE,{"derivedFrom":subQ2}),1.0]])]});}
            var Q6;
            {var subQ1=sQuery(id+"F0.wireOp",EDGE,"E43.trimOffspring");var subQ3=makeQuery(id+"F1.opExtrude","SWEPT_EDGE",EDGE,{"disambiguationData":[OSD([subQ1,sQuery(id+"F0.wireOp",EDGE,"E57")])]});Q6=makeQuery(id+"F6.imprint","IMPRINT",FACE,{"disambiguationData":[TD([[makeQuery(id+"F6.imprint","IMPRINT",EDGE,{"derivedFrom":subQ3}),1.0]])]});}
            var Q7;
            {var subQ0=sQuery(id+"F6.wireOp",EDGE,"E96.top");Q7=makeQuery(id+"F6.imprint","IMPRINT",FACE,{"disambiguationData":[TD([[makeQuery(id+"F6.imprint","IMPRINT",EDGE,{"derivedFrom":subQ0}),1.0]])]});}
            var Q8;
            {var subQ1=sQuery(id+"F0.wireOp",EDGE,"E45.trimOffspring");var subQ3=makeQuery(id+"F1.opExtrude","SWEPT_EDGE",EDGE,{"disambiguationData":[OSD([subQ1,sQuery(id+"F0.wireOp",EDGE,"E54.trimOffspring")])]});Q8=makeQuery(id+"F6.imprint","IMPRINT",FACE,{"disambiguationData":[TD([[makeQuery(id+"F6.imprint","IMPRINT",EDGE,{"derivedFrom":subQ3}),-1.0]])]});}
            var Q9;
            {var subQ1=sQuery(id+"F0.wireOp",EDGE,"E41.trimOffspring");var subQ2=makeQuery(id+"F1.opExtrude","SWEPT_EDGE",EDGE,{"disambiguationData":[OSD([sQuery(id+"F0.wireOp",EDGE,"E4"),subQ1])]});Q9=makeQuery(id+"F6.imprint","IMPRINT",FACE,{"disambiguationData":[TD([[makeQuery(id+"F6.imprint","IMPRINT",EDGE,{"derivedFrom":subQ2}),-1.0]])]});}
            var Q10;
            {var subQ3=sQuery(id+"F0.wireOp",EDGE,"E43.trimOffspring");var subQ5=sQuery(id+"F0.wireOp",EDGE,"E66");var subQ6=makeQuery(id+"F1.opExtrude","SWEPT_EDGE",EDGE,{"disambiguationData":[OSD([subQ3,subQ5])]});Q10=makeQuery(id+"F6.imprint","IMPRINT",FACE,{"disambiguationData":[TD([[makeQuery(id+"F6.imprint","IMPRINT",EDGE,{"derivedFrom":subQ6}),-1.0]])]});}
            var Q11;
            {var subQ1=sQuery(id+"F0.wireOp",EDGE,"E67");var subQ2=sQuery(id+"F0.wireOp",EDGE,"E43.trimOffspring");var subQ3=makeQuery(id+"F1.opExtrude","SWEPT_EDGE",EDGE,{"disambiguationData":[OSD([subQ2,subQ1])]});Q11=makeQuery(id+"F6.imprint","IMPRINT",FACE,{"disambiguationData":[TD([[makeQuery(id+"F6.imprint","IMPRINT",EDGE,{"derivedFrom":subQ3}),1.0]])]});}
            var Q12;
            {var subQ1=sQuery(id+"F0.wireOp",EDGE,"E58");var subQ2=sQuery(id+"F0.wireOp",EDGE,"E43.trimOffspring");var subQ3=makeQuery(id+"F1.opExtrude","SWEPT_EDGE",EDGE,{"disambiguationData":[OSD([subQ2,subQ1])]});Q12=makeQuery(id+"F6.imprint","IMPRINT",FACE,{"disambiguationData":[TD([[makeQuery(id+"F6.imprint","IMPRINT",EDGE,{"derivedFrom":subQ3}),-1.0]])]});}
            var Q13;
            {var subQ14=sQuery(id+"F2.wireOp",EDGE,"E77");var subQ37=makeQuery(id+"F3.opExtrude","CAP_EDGE",EDGE,{"disambiguationData":[OSD([subQ14])],"isStart":false});Q13=makeQuery(id+"F6.imprint","IMPRINT",FACE,{"disambiguationData":[TD([[makeQuery(id+"F6.imprint","IMPRINT",EDGE,{"derivedFrom":subQ37}),1.0]])]});}
            var Q14;
            {var subQ80=sQuery(id+"F6.wireOp",EDGE,"E96.bottom");Q14=makeQuery(id+"F6.imprint","IMPRINT",FACE,{"disambiguationData":[TD([[makeQuery(id+"F6.imprint","IMPRINT",EDGE,{"derivedFrom":subQ80}),1.0]])]});}
            extrude(context, id + "F7", {"entities" : qUnion([Q0, Q1, Q2, Q3, Q4, Q5, Q6, Q7, Q8, Q9, Q10, Q11, Q12, Q13, Q14]), "operationType" : NewBodyOperationType.ADD, "depth" : 12 * mm, "offsetDistance" : 25 * mm, "symmetric" : true});
        }
        {
            var Q0;
            {var subQ0=sQuery(id+"F2.wireOp",EDGE,"E77");Q0=makeQuery(id+"F7.boolean.opBoolean","MERGE",FACE,{"derivedFrom":[makeQuery(id+"F3.opExtrude","CAP_FACE",FACE,{"disambiguationData":[OSD([sQuery(id+"F2.wireOp",EDGE,"E76"),subQ0,sQuery(id+"F2.wireOp",EDGE,"E78"),sQuery(id+"F2.wireOp",EDGE,"E79"),sQuery(id+"F2.wireOp",EDGE,"E80"),sQuery(id+"F2.wireOp",EDGE,"E83.bottom"),sQuery(id+"F2.wireOp",EDGE,"E83.top"),sQuery(id+"F2.wireOp",EDGE,"E83.left"),sQuery(id+"F2.wireOp",EDGE,"E83.right"),sQuery(id+"F2.wireOp",EDGE,"E84.bottom"),sQuery(id+"F2.wireOp",EDGE,"E84.top"),sQuery(id+"F2.wireOp",EDGE,"E84.left"),sQuery(id+"F2.wireOp",EDGE,"E84.right"),sQuery(id+"F2.wireOp",EDGE,"E85.bottom"),sQuery(id+"F2.wireOp",EDGE,"E85.top"),sQuery(id+"F2.wireOp",EDGE,"E85.left"),sQuery(id+"F2.wireOp",EDGE,"E85.right")])],"isStart":false}),makeQuery(id+"F7.opExtrude","SWEPT_FACE",FACE,{"disambiguationData":[OSD([subQ0])]})]});}
            var sketch = newSketch(context, id + "F8", { "sketchPlane" : qUnion([Q0])});
            skLineSegment(sketch, "E97.bottom", {"start": v(0, 0) * mm, "end": v(-100, 0) * mm});
            skLineSegment(sketch, "E97.top", {"start": v(0, 2550) * mm, "end": v(-100, 2550) * mm});
            skLineSegment(sketch, "E97.left", {"start": v(0, 0) * mm, "end": v(0, 2550) * mm});
            skLineSegment(sketch, "E97.right", {"start": v(-100, 0) * mm, "end": v(-100, 2550) * mm});
            skSolve(sketch);
        }
        {
            var Q0;
            Q0 = qSketchRegion(id + "F8", true);
            extrude(context, id + "F9", {"entities" : qUnion([Q0]), "operationType" : NewBodyOperationType.ADD, "depth" : 4400 * mm, "offsetDistance" : 25 * mm});
        }
        {
            var Q0;
            Q0=makeQuery(id+"F9.opExtrude","SWEPT_FACE",FACE,{"disambiguationData":[OSD([sQuery(id+"F8.wireOp",EDGE,"E97.right")])]});
            var sketch = newSketch(context, id + "F10", { "sketchPlane" : qUnion([Q0])});
            skLineSegment(sketch, "E98.bottom", {"start": v(12, 2500) * mm, "end": v(512, 2500) * mm});
            skLineSegment(sketch, "E98.top", {"start": v(12, 2050) * mm, "end": v(512, 2050) * mm});
            skLineSegment(sketch, "E98.left", {"start": v(12, 2500) * mm, "end": v(12, 2050) * mm});
            skLineSegment(sketch, "E98.right", {"start": v(512, 2500) * mm, "end": v(512, 2050) * mm});
            skLineSegment(sketch, "E99.1.0.0", {"start": v(562, 2500) * mm, "end": v(1062, 2500) * mm});
            skLineSegment(sketch, "E99.1.0.1", {"start": v(562, 2050) * mm, "end": v(1062, 2050) * mm});
            skLineSegment(sketch, "E99.1.0.2", {"start": v(562, 2500) * mm, "end": v(562, 2050) * mm});
            skLineSegment(sketch, "E99.1.0.3", {"start": v(1062, 2500) * mm, "end": v(1062, 2050) * mm});
            skLineSegment(sketch, "E99.2.0.0", {"start": v(1112, 2500) * mm, "end": v(1612, 2500) * mm});
            skLineSegment(sketch, "E99.2.0.1", {"start": v(1112, 2050) * mm, "end": v(1612, 2050) * mm});
            skLineSegment(sketch, "E99.2.0.2", {"start": v(1112, 2500) * mm, "end": v(1112, 2050) * mm});
            skLineSegment(sketch, "E99.2.0.3", {"start": v(1612, 2500) * mm, "end": v(1612, 2050) * mm});
            skLineSegment(sketch, "E99.3.0.0", {"start": v(1662, 2500) * mm, "end": v(2162, 2500) * mm});
            skLineSegment(sketch, "E99.3.0.1", {"start": v(1662, 2050) * mm, "end": v(2162, 2050) * mm});
            skLineSegment(sketch, "E99.3.0.2", {"start": v(1662, 2500) * mm, "end": v(1662, 2050) * mm});
            skLineSegment(sketch, "E99.3.0.3", {"start": v(2162, 2500) * mm, "end": v(2162, 2050) * mm});
            skLineSegment(sketch, "E99.4.0.0", {"start": v(2212, 2500) * mm, "end": v(2712, 2500) * mm});
            skLineSegment(sketch, "E99.4.0.1", {"start": v(2212, 2050) * mm, "end": v(2712, 2050) * mm});
            skLineSegment(sketch, "E99.4.0.2", {"start": v(2212, 2500) * mm, "end": v(2212, 2050) * mm});
            skLineSegment(sketch, "E99.4.0.3", {"start": v(2712, 2500) * mm, "end": v(2712, 2050) * mm});
            skLineSegment(sketch, "E99.5.0.0", {"start": v(2762, 2500) * mm, "end": v(3262, 2500) * mm});
            skLineSegment(sketch, "E99.5.0.1", {"start": v(2762, 2050) * mm, "end": v(3262, 2050) * mm});
            skLineSegment(sketch, "E99.5.0.2", {"start": v(2762, 2500) * mm, "end": v(2762, 2050) * mm});
            skLineSegment(sketch, "E99.5.0.3", {"start": v(3262, 2500) * mm, "end": v(3262, 2050) * mm});
            skLineSegment(sketch, "E99.6.0.0", {"start": v(3312, 2500) * mm, "end": v(3812, 2500) * mm});
            skLineSegment(sketch, "E99.6.0.1", {"start": v(3312, 2050) * mm, "end": v(3812, 2050) * mm});
            skLineSegment(sketch, "E99.6.0.2", {"start": v(3312, 2500) * mm, "end": v(3312, 2050) * mm});
            skLineSegment(sketch, "E99.6.0.3", {"start": v(3812, 2500) * mm, "end": v(3812, 2050) * mm});
            skLineSegment(sketch, "E99.7.0.0", {"start": v(3862, 2500) * mm, "end": v(4362, 2500) * mm});
            skLineSegment(sketch, "E99.7.0.1", {"start": v(3862, 2050) * mm, "end": v(4362, 2050) * mm});
            skLineSegment(sketch, "E99.7.0.2", {"start": v(3862, 2500) * mm, "end": v(3862, 2050) * mm});
            skLineSegment(sketch, "E99.7.0.3", {"start": v(4362, 2500) * mm, "end": v(4362, 2050) * mm});
            skLineSegment(sketch, "E99.direction1", {"start": v(12, 2050) * mm, "end": v(562, 2050) * mm, "construction": true});
            skSolve(sketch);
        }
        {
            var Q0;
            Q0 = qSketchRegion(id + "F10", true);
            extrude(context, id + "F11", {"entities" : qUnion([Q0]), "operationType" : NewBodyOperationType.REMOVE, "oppositeDirection" : true, "depth" : 100 * mm, "offsetDistance" : 25 * mm});
        }
    });
